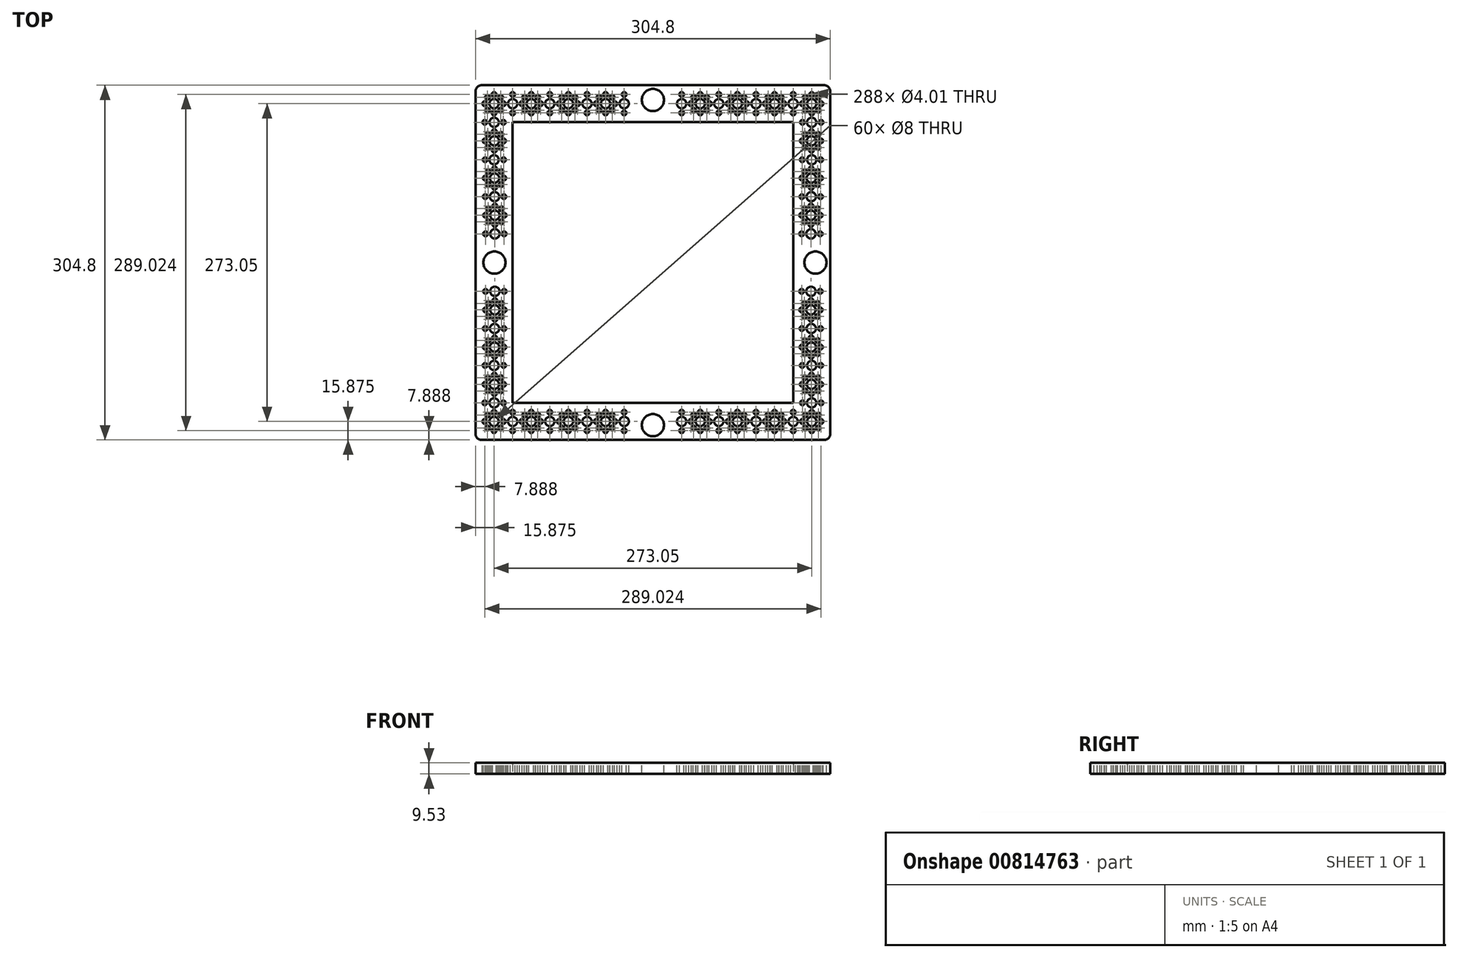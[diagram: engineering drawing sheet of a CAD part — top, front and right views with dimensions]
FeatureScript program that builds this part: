
annotation { "Feature Type Name" : "Feature", "Feature Type Description" : "" }
export const myFeature = defineFeature(function(context is Context, id is Id, definition is map)
    precondition{}
    {
        {
            var Q0;
            Q0=qCreatedBy(makeId("Top.planeOp"),FACE);
            var sketch = newSketch(context, id + "F0", { "sketchPlane" : qUnion([Q0])});
            skLineSegment(sketch, "E0.bottom", {"start": v(152.4, 152.4) * mm, "end": v(-152.4, 152.4) * mm});
            skLineSegment(sketch, "E0.top", {"start": v(152.4, -152.4) * mm, "end": v(-152.4, -152.4) * mm});
            skLineSegment(sketch, "E0.left", {"start": v(152.4, 152.4) * mm, "end": v(152.4, -152.4) * mm});
            skLineSegment(sketch, "E0.right", {"start": v(-152.4, 152.4) * mm, "end": v(-152.4, -152.4) * mm});
            skPoint(sketch, "E0.middle", {"position": v(0, 0) * mm});
            skLineSegment(sketch, "E1.bottom", {"start": v(-120.65, 120.65) * mm, "end": v(120.65, 120.65) * mm});
            skLineSegment(sketch, "E1.top", {"start": v(-120.65, -120.65) * mm, "end": v(120.65, -120.65) * mm});
            skLineSegment(sketch, "E1.left", {"start": v(-120.65, 120.65) * mm, "end": v(-120.65, -120.65) * mm});
            skLineSegment(sketch, "E1.right", {"start": v(120.65, 120.65) * mm, "end": v(120.65, -120.65) * mm});
            skSolve(sketch);
        }
        {
            var Q0;
            Q0=qSketchRegion(id+"F0",true);
            extrude(context, id + "F1", {"entities" : qUnion([Q0]), "depth" : 9.52 * mm, "offsetDistance" : 25.4 * mm});
        }
        {
            var Q0;
            Q0=makeQuery(id+"F1.opExtrude","CAP_FACE",FACE,{"disambiguationData":[OSD([sQuery(id+"F0.wireOp",EDGE,"E0.bottom"),sQuery(id+"F0.wireOp",EDGE,"E0.top"),sQuery(id+"F0.wireOp",EDGE,"E0.left"),sQuery(id+"F0.wireOp",EDGE,"E0.right")])],"isStart":false});
            var sketch = newSketch(context, id + "F2", { "sketchPlane" : qUnion([Q0])});
            skPoint(sketch, "E2", {"position": v(0, 139.7) * mm});
            skPoint(sketch, "E3", {"position": v(139.7, 0) * mm});
            skPoint(sketch, "E4", {"position": v(0, -139.7) * mm});
            skPoint(sketch, "E5", {"position": v(-136.2, 0) * mm});
            skLineSegment(sketch, "E6", {"start": v(0, 120.65) * mm, "end": v(0, 152.4) * mm});
            skSolve(sketch);
        }
        {
            var Q0;
            Q0=sQuery(id+"F2.wireOp",VERTEX,"E2");
            var Q1;
            Q1=sQuery(id+"F2.wireOp",VERTEX,"E3");
            var Q2;
            Q2=sQuery(id+"F2.wireOp",VERTEX,"E4");
            var Q3;
            Q3=sQuery(id+"F2.wireOp",VERTEX,"E5");
            var Q4;
            Q4=makeQuery(id+"F1.opExtrude","SWEPT_BODY",BODY,{"disambiguationData":[OSD([sQuery(id+"F0.wireOp",EDGE,"E0.bottom"),sQuery(id+"F0.wireOp",EDGE,"E0.top"),sQuery(id+"F0.wireOp",EDGE,"E0.left"),sQuery(id+"F0.wireOp",EDGE,"E0.right")])]});
            hole(context, id + "F3", {"style" : HoleStyle.SIMPLE, "endStyle" : HoleEndStyle.THROUGH, "holeDiameter" : 19.05 * mm, "locations" : qUnion([Q0, Q1, Q2, Q3]), "scope" : qUnion([Q4]), "tappedDepth" : 12.7 * mm, "tapClearance" : 3, "majorDiameter" : 6.35 * mm});
        }
        {
            var Q0;
            Q0=makeQuery(id+"F1.opExtrude","SWEPT_EDGE",EDGE,{"disambiguationData":[OSD([sQuery(id+"F0.wireOp",EDGE,"E0.bottom"),sQuery(id+"F0.wireOp",EDGE,"E0.right")])]});
            fillet(context, id + "F4", {"entities" : qUnion([Q0]), "radius" : 5.08 * mm, "tangentPropagation" : true, "allowEdgeOverflow" : false});
        }
        {
            var Q0;
            Q0=makeQuery(id+"F1.opExtrude","SWEPT_EDGE",EDGE,{"disambiguationData":[OSD([sQuery(id+"F0.wireOp",EDGE,"E0.bottom"),sQuery(id+"F0.wireOp",EDGE,"E0.left")])]});
            var Q1;
            Q1=makeQuery(id+"F1.opExtrude","SWEPT_EDGE",EDGE,{"disambiguationData":[OSD([sQuery(id+"F0.wireOp",EDGE,"E0.top"),sQuery(id+"F0.wireOp",EDGE,"E0.left")])]});
            var Q2;
            Q2=makeQuery(id+"F1.opExtrude","SWEPT_EDGE",EDGE,{"disambiguationData":[OSD([sQuery(id+"F0.wireOp",EDGE,"E0.top"),sQuery(id+"F0.wireOp",EDGE,"E0.right")])]});
            fillet(context, id + "F5", {"entities" : qUnion([Q0, Q1, Q2]), "radius" : 5.08 * mm, "tangentPropagation" : true, "allowEdgeOverflow" : false});
        }
        {
            var Q0;
            Q0=makeQuery(id+"F1.opExtrude","CAP_FACE",FACE,{"disambiguationData":[OSD([sQuery(id+"F0.wireOp",EDGE,"E0.bottom"),sQuery(id+"F0.wireOp",EDGE,"E0.top"),sQuery(id+"F0.wireOp",EDGE,"E0.left"),sQuery(id+"F0.wireOp",EDGE,"E0.right")])],"isStart":false});
            var sketch = newSketch(context, id + "F6", { "sketchPlane" : qUnion([Q0])});
            skPoint(sketch, "E7", {"position": v(-136.53, 136.53) * mm});
            skPoint(sketch, "E8", {"position": v(-136.53, 144.51) * mm});
            skPoint(sketch, "E9.1.0", {"position": v(-142.17, 142.17) * mm});
            skPoint(sketch, "E9.2.0", {"position": v(-144.51, 136.52) * mm});
            skPoint(sketch, "E9.3.0", {"position": v(-142.17, 130.88) * mm});
            skPoint(sketch, "E9.4.0", {"position": v(-136.53, 128.54) * mm});
            skPoint(sketch, "E9.5.0", {"position": v(-130.88, 130.88) * mm});
            skPoint(sketch, "E9.6.0", {"position": v(-128.54, 136.53) * mm});
            skPoint(sketch, "E9.7.0", {"position": v(-130.88, 142.17) * mm});
            skPoint(sketch, "E10.1.0.0", {"position": v(-104.58, 136.53) * mm});
            skPoint(sketch, "E10.1.0.1", {"position": v(-104.58, 144.51) * mm});
            skPoint(sketch, "E10.1.0.2", {"position": v(-110.22, 142.17) * mm});
            skPoint(sketch, "E10.1.0.3", {"position": v(-112.56, 136.52) * mm});
            skPoint(sketch, "E10.1.0.4", {"position": v(-110.22, 130.88) * mm});
            skPoint(sketch, "E10.1.0.5", {"position": v(-104.58, 128.54) * mm});
            skPoint(sketch, "E10.1.0.6", {"position": v(-98.93, 130.88) * mm});
            skPoint(sketch, "E10.1.0.7", {"position": v(-96.59, 136.53) * mm});
            skPoint(sketch, "E10.1.0.8", {"position": v(-98.93, 142.17) * mm});
            skPoint(sketch, "E10.2.0.0", {"position": v(-72.63, 136.53) * mm});
            skPoint(sketch, "E10.2.0.1", {"position": v(-72.63, 144.51) * mm});
            skPoint(sketch, "E10.2.0.2", {"position": v(-78.28, 142.17) * mm});
            skPoint(sketch, "E10.2.0.3", {"position": v(-80.62, 136.52) * mm});
            skPoint(sketch, "E10.2.0.4", {"position": v(-78.28, 130.88) * mm});
            skPoint(sketch, "E10.2.0.5", {"position": v(-72.63, 128.54) * mm});
            skPoint(sketch, "E10.2.0.6", {"position": v(-66.98, 130.88) * mm});
            skPoint(sketch, "E10.2.0.7", {"position": v(-64.64, 136.53) * mm});
            skPoint(sketch, "E10.2.0.8", {"position": v(-66.98, 142.17) * mm});
            skPoint(sketch, "E10.3.0.0", {"position": v(-40.68, 136.53) * mm});
            skPoint(sketch, "E10.3.0.1", {"position": v(-40.68, 144.51) * mm});
            skPoint(sketch, "E10.3.0.2", {"position": v(-46.33, 142.17) * mm});
            skPoint(sketch, "E10.3.0.3", {"position": v(-48.67, 136.52) * mm});
            skPoint(sketch, "E10.3.0.4", {"position": v(-46.33, 130.88) * mm});
            skPoint(sketch, "E10.3.0.5", {"position": v(-40.68, 128.54) * mm});
            skPoint(sketch, "E10.3.0.6", {"position": v(-35.03, 130.88) * mm});
            skPoint(sketch, "E10.3.0.7", {"position": v(-32.7, 136.53) * mm});
            skPoint(sketch, "E10.3.0.8", {"position": v(-35.03, 142.17) * mm});
            skLineSegment(sketch, "E10.direction1", {"start": v(-136.53, 136.53) * mm, "end": v(-104.58, 136.53) * mm, "construction": true});
            skPoint(sketch, "E11", {"position": v(-120.55, 136.53) * mm});
            skPoint(sketch, "E12", {"position": v(-88.6, 136.53) * mm});
            skPoint(sketch, "E13", {"position": v(-24.7, 136.53) * mm});
            skPoint(sketch, "E14", {"position": v(-56.65, 136.53) * mm});
            skPoint(sketch, "E15", {"position": v(-56.65, 144.51) * mm});
            skPoint(sketch, "E16", {"position": v(-24.7, 144.51) * mm});
            skPoint(sketch, "E17", {"position": v(-24.7, 128.54) * mm});
            skPoint(sketch, "E18", {"position": v(-56.65, 128.54) * mm});
            skPoint(sketch, "E19", {"position": v(-88.6, 128.54) * mm});
            skPoint(sketch, "E20", {"position": v(-88.6, 144.51) * mm});
            skPoint(sketch, "E21", {"position": v(-120.55, 128.54) * mm});
            skPoint(sketch, "E22", {"position": v(-120.55, 144.51) * mm});
            skPoint(sketch, "E23.MirrorP", {"position": v(96.59, 136.53) * mm});
            skLineSegment(sketch, "E24.MirrorCS", {"start": v(136.53, 136.53) * mm, "end": v(104.58, 136.53) * mm, "construction": true});
            skPoint(sketch, "E25.MirrorP", {"position": v(48.67, 136.52) * mm});
            skPoint(sketch, "E26.MirrorP", {"position": v(64.64, 136.53) * mm});
            skPoint(sketch, "E27.MirrorP", {"position": v(88.6, 136.53) * mm});
            skPoint(sketch, "E28.MirrorP", {"position": v(40.68, 136.53) * mm});
            skPoint(sketch, "E29.MirrorP", {"position": v(32.7, 136.53) * mm});
            skPoint(sketch, "E30.MirrorP", {"position": v(136.53, 136.53) * mm});
            skPoint(sketch, "E31.MirrorP", {"position": v(120.55, 136.53) * mm});
            skPoint(sketch, "E32.MirrorP", {"position": v(98.93, 130.88) * mm});
            skPoint(sketch, "E33.MirrorP", {"position": v(78.28, 142.17) * mm});
            skPoint(sketch, "E34.MirrorP", {"position": v(46.33, 130.88) * mm});
            skPoint(sketch, "E35.MirrorP", {"position": v(120.55, 128.54) * mm});
            skPoint(sketch, "E36.MirrorP", {"position": v(78.28, 130.88) * mm});
            skPoint(sketch, "E37.MirrorP", {"position": v(66.98, 130.88) * mm});
            skPoint(sketch, "E38.MirrorP", {"position": v(110.22, 130.88) * mm});
            skPoint(sketch, "E39.MirrorP", {"position": v(130.88, 142.17) * mm});
            skPoint(sketch, "E40.MirrorP", {"position": v(144.51, 136.52) * mm});
            skPoint(sketch, "E41.MirrorP", {"position": v(56.65, 128.54) * mm});
            skPoint(sketch, "E42.MirrorP", {"position": v(72.63, 136.53) * mm});
            skPoint(sketch, "E43.MirrorP", {"position": v(142.17, 130.88) * mm});
            skPoint(sketch, "E44.MirrorP", {"position": v(40.68, 128.54) * mm});
            skPoint(sketch, "E45.MirrorP", {"position": v(104.58, 144.51) * mm});
            skPoint(sketch, "E46.MirrorP", {"position": v(120.55, 144.51) * mm});
            skPoint(sketch, "E47.MirrorP", {"position": v(98.93, 142.17) * mm});
            skPoint(sketch, "E48.MirrorP", {"position": v(104.58, 128.54) * mm});
            skPoint(sketch, "E49.MirrorP", {"position": v(56.65, 136.53) * mm});
            skPoint(sketch, "E50.MirrorP", {"position": v(72.63, 128.54) * mm});
            skPoint(sketch, "E51.MirrorP", {"position": v(80.62, 136.52) * mm});
            skPoint(sketch, "E52.MirrorP", {"position": v(24.7, 144.51) * mm});
            skPoint(sketch, "E53.MirrorP", {"position": v(35.03, 130.88) * mm});
            skPoint(sketch, "E54.MirrorP", {"position": v(24.7, 128.54) * mm});
            skPoint(sketch, "E55.MirrorP", {"position": v(66.98, 142.17) * mm});
            skPoint(sketch, "E56.MirrorP", {"position": v(72.63, 144.51) * mm});
            skPoint(sketch, "E57.MirrorP", {"position": v(40.68, 144.51) * mm});
            skPoint(sketch, "E58.MirrorP", {"position": v(88.6, 128.54) * mm});
            skPoint(sketch, "E59.MirrorP", {"position": v(35.03, 142.17) * mm});
            skPoint(sketch, "E60.MirrorP", {"position": v(24.7, 136.53) * mm});
            skPoint(sketch, "E61.MirrorP", {"position": v(56.65, 144.51) * mm});
            skPoint(sketch, "E62.MirrorP", {"position": v(46.33, 142.17) * mm});
            skPoint(sketch, "E63.MirrorP", {"position": v(88.6, 144.51) * mm});
            skPoint(sketch, "E64.MirrorP", {"position": v(104.58, 136.53) * mm});
            skPoint(sketch, "E65.MirrorP", {"position": v(128.54, 136.53) * mm});
            skPoint(sketch, "E66.MirrorP", {"position": v(130.88, 130.88) * mm});
            skPoint(sketch, "E67.MirrorP", {"position": v(136.53, 128.54) * mm});
            skPoint(sketch, "E68.MirrorP", {"position": v(136.53, 144.51) * mm});
            skPoint(sketch, "E69.MirrorP", {"position": v(142.17, 142.17) * mm});
            skPoint(sketch, "E70.MirrorP", {"position": v(110.22, 142.17) * mm});
            skPoint(sketch, "E71.MirrorP", {"position": v(112.56, 136.52) * mm});
            skPoint(sketch, "E72.MirrorP", {"position": v(144.51, -136.52) * mm});
            skPoint(sketch, "E73.MirrorP", {"position": v(-88.6, -136.53) * mm});
            skPoint(sketch, "E74.MirrorP", {"position": v(-80.62, -136.52) * mm});
            skPoint(sketch, "E75.MirrorP", {"position": v(-48.67, -136.52) * mm});
            skPoint(sketch, "E76.MirrorP", {"position": v(-40.68, -136.53) * mm});
            skPoint(sketch, "E77.MirrorP", {"position": v(136.53, -136.53) * mm});
            skLineSegment(sketch, "E78.MirrorCS", {"start": v(-136.53, -136.53) * mm, "end": v(-104.58, -136.53) * mm, "construction": true});
            skLineSegment(sketch, "E79.MirrorCS", {"start": v(136.53, -136.53) * mm, "end": v(104.58, -136.53) * mm, "construction": true});
            skPoint(sketch, "E80.MirrorP", {"position": v(-136.53, -136.53) * mm});
            skPoint(sketch, "E81.MirrorP", {"position": v(104.58, -136.53) * mm});
            skPoint(sketch, "E82.MirrorP", {"position": v(-78.28, -142.17) * mm});
            skPoint(sketch, "E83.MirrorP", {"position": v(-96.59, -136.53) * mm});
            skPoint(sketch, "E84.MirrorP", {"position": v(96.59, -136.53) * mm});
            skPoint(sketch, "E85.MirrorP", {"position": v(-136.53, -144.51) * mm});
            skPoint(sketch, "E86.MirrorP", {"position": v(-104.58, -136.53) * mm});
            skPoint(sketch, "E87.MirrorP", {"position": v(120.55, -136.53) * mm});
            skPoint(sketch, "E88.MirrorP", {"position": v(142.17, -142.17) * mm});
            skPoint(sketch, "E89.MirrorP", {"position": v(-110.22, -142.17) * mm});
            skPoint(sketch, "E90.MirrorP", {"position": v(-24.7, -136.53) * mm});
            skPoint(sketch, "E91.MirrorP", {"position": v(-72.63, -144.51) * mm});
            skPoint(sketch, "E92.MirrorP", {"position": v(72.63, -136.53) * mm});
            skPoint(sketch, "E93.MirrorP", {"position": v(56.65, -136.53) * mm});
            skPoint(sketch, "E94.MirrorP", {"position": v(56.65, -144.51) * mm});
            skPoint(sketch, "E95.MirrorP", {"position": v(-112.56, -136.52) * mm});
            skPoint(sketch, "E96.MirrorP", {"position": v(-56.65, -136.53) * mm});
            skPoint(sketch, "E97.MirrorP", {"position": v(-40.68, -144.51) * mm});
            skPoint(sketch, "E98.MirrorP", {"position": v(64.64, -136.53) * mm});
            skPoint(sketch, "E99.MirrorP", {"position": v(-32.7, -136.53) * mm});
            skPoint(sketch, "E100.MirrorP", {"position": v(88.6, -144.51) * mm});
            skPoint(sketch, "E101.MirrorP", {"position": v(104.58, -144.51) * mm});
            skPoint(sketch, "E102.MirrorP", {"position": v(110.22, -130.88) * mm});
            skPoint(sketch, "E103.MirrorP", {"position": v(-120.55, -128.54) * mm});
            skPoint(sketch, "E104.MirrorP", {"position": v(32.7, -136.53) * mm});
            skPoint(sketch, "E105.MirrorP", {"position": v(-104.58, -128.54) * mm});
            skPoint(sketch, "E106.MirrorP", {"position": v(-35.03, -142.17) * mm});
            skPoint(sketch, "E107.MirrorP", {"position": v(80.62, -136.52) * mm});
            skPoint(sketch, "E108.MirrorP", {"position": v(-78.28, -130.88) * mm});
            skPoint(sketch, "E109.MirrorP", {"position": v(120.55, -144.51) * mm});
            skPoint(sketch, "E110.MirrorP", {"position": v(-98.93, -130.88) * mm});
            skPoint(sketch, "E111.MirrorP", {"position": v(-56.65, -144.51) * mm});
            skPoint(sketch, "E112.MirrorP", {"position": v(98.93, -130.88) * mm});
            skPoint(sketch, "E113.MirrorP", {"position": v(-72.63, -136.53) * mm});
            skPoint(sketch, "E114.MirrorP", {"position": v(72.63, -128.54) * mm});
            skPoint(sketch, "E115.MirrorP", {"position": v(128.54, -136.53) * mm});
            skPoint(sketch, "E116.MirrorP", {"position": v(-98.93, -142.17) * mm});
            skPoint(sketch, "E117.MirrorP", {"position": v(-35.03, -130.88) * mm});
            skPoint(sketch, "E118.MirrorP", {"position": v(-66.98, -142.17) * mm});
            skPoint(sketch, "E119.MirrorP", {"position": v(48.67, -136.52) * mm});
            skPoint(sketch, "E120.MirrorP", {"position": v(-24.7, -128.54) * mm});
            skPoint(sketch, "E121.MirrorP", {"position": v(56.65, -128.54) * mm});
            skPoint(sketch, "E122.MirrorP", {"position": v(46.33, -130.88) * mm});
            skPoint(sketch, "E123.MirrorP", {"position": v(40.68, -136.53) * mm});
            skPoint(sketch, "E124.MirrorP", {"position": v(40.68, -128.54) * mm});
            skPoint(sketch, "E125.MirrorP", {"position": v(24.7, -136.53) * mm});
            skPoint(sketch, "E126.MirrorP", {"position": v(136.53, -144.51) * mm});
            skPoint(sketch, "E127.MirrorP", {"position": v(88.6, -136.53) * mm});
            skPoint(sketch, "E128.MirrorP", {"position": v(142.17, -130.88) * mm});
            skPoint(sketch, "E129.MirrorP", {"position": v(35.03, -142.17) * mm});
            skPoint(sketch, "E130.MirrorP", {"position": v(-142.17, -142.17) * mm});
            skPoint(sketch, "E131.MirrorP", {"position": v(-40.68, -128.54) * mm});
            skPoint(sketch, "E132.MirrorP", {"position": v(-64.64, -136.53) * mm});
            skPoint(sketch, "E133.MirrorP", {"position": v(-24.7, -144.51) * mm});
            skPoint(sketch, "E134.MirrorP", {"position": v(78.28, -142.17) * mm});
            skPoint(sketch, "E135.MirrorP", {"position": v(24.7, -144.51) * mm});
            skPoint(sketch, "E136.MirrorP", {"position": v(136.53, -128.54) * mm});
            skPoint(sketch, "E137.MirrorP", {"position": v(120.55, -128.54) * mm});
            skPoint(sketch, "E138.MirrorP", {"position": v(46.33, -142.17) * mm});
            skPoint(sketch, "E139.MirrorP", {"position": v(-66.98, -130.88) * mm});
            skPoint(sketch, "E140.MirrorP", {"position": v(-120.55, -144.51) * mm});
            skPoint(sketch, "E141.MirrorP", {"position": v(130.88, -142.17) * mm});
            skPoint(sketch, "E142.MirrorP", {"position": v(-88.6, -128.54) * mm});
            skPoint(sketch, "E143.MirrorP", {"position": v(104.58, -128.54) * mm});
            skPoint(sketch, "E144.MirrorP", {"position": v(-110.22, -130.88) * mm});
            skPoint(sketch, "E145.MirrorP", {"position": v(-46.33, -142.17) * mm});
            skPoint(sketch, "E146.MirrorP", {"position": v(-88.6, -144.51) * mm});
            skPoint(sketch, "E147.MirrorP", {"position": v(66.98, -130.88) * mm});
            skPoint(sketch, "E148.MirrorP", {"position": v(40.68, -144.51) * mm});
            skPoint(sketch, "E149.MirrorP", {"position": v(-120.55, -136.53) * mm});
            skPoint(sketch, "E150.MirrorP", {"position": v(35.03, -130.88) * mm});
            skPoint(sketch, "E151.MirrorP", {"position": v(-130.88, -142.17) * mm});
            skPoint(sketch, "E152.MirrorP", {"position": v(-128.54, -136.53) * mm});
            skPoint(sketch, "E153.MirrorP", {"position": v(-130.88, -130.88) * mm});
            skPoint(sketch, "E154.MirrorP", {"position": v(-136.53, -128.54) * mm});
            skPoint(sketch, "E155.MirrorP", {"position": v(-142.17, -130.88) * mm});
            skPoint(sketch, "E156.MirrorP", {"position": v(-144.51, -136.52) * mm});
            skPoint(sketch, "E157.MirrorP", {"position": v(72.63, -144.51) * mm});
            skPoint(sketch, "E158.MirrorP", {"position": v(112.56, -136.52) * mm});
            skPoint(sketch, "E159.MirrorP", {"position": v(66.98, -142.17) * mm});
            skPoint(sketch, "E160.MirrorP", {"position": v(78.28, -130.88) * mm});
            skPoint(sketch, "E161.MirrorP", {"position": v(-72.63, -128.54) * mm});
            skPoint(sketch, "E162.MirrorP", {"position": v(98.93, -142.17) * mm});
            skPoint(sketch, "E163.MirrorP", {"position": v(-104.58, -144.51) * mm});
            skPoint(sketch, "E164.MirrorP", {"position": v(24.7, -128.54) * mm});
            skPoint(sketch, "E165.MirrorP", {"position": v(-56.65, -128.54) * mm});
            skPoint(sketch, "E166.MirrorP", {"position": v(130.88, -130.88) * mm});
            skPoint(sketch, "E167.MirrorP", {"position": v(-46.33, -130.88) * mm});
            skPoint(sketch, "E168.MirrorP", {"position": v(88.6, -128.54) * mm});
            skPoint(sketch, "E169.MirrorP", {"position": v(110.22, -142.17) * mm});
            skPoint(sketch, "E170.1.0.0", {"position": v(-136.3, -104.58) * mm});
            skPoint(sketch, "E170.1.0.1", {"position": v(-144.28, -104.58) * mm});
            skPoint(sketch, "E170.1.0.2", {"position": v(-141.94, -110.23) * mm});
            skPoint(sketch, "E170.1.0.3", {"position": v(-141.94, -98.93) * mm});
            skPoint(sketch, "E170.1.0.4", {"position": v(-136.3, -96.6) * mm});
            skPoint(sketch, "E170.1.0.5", {"position": v(-136.3, -112.56) * mm});
            skPoint(sketch, "E170.1.0.6", {"position": v(-130.65, -110.23) * mm});
            skPoint(sketch, "E170.1.0.7", {"position": v(-128.3, -104.58) * mm});
            skPoint(sketch, "E170.1.0.8", {"position": v(-130.65, -98.93) * mm});
            skPoint(sketch, "E170.2.0.0", {"position": v(-136.06, -72.63) * mm});
            skPoint(sketch, "E170.2.0.1", {"position": v(-144.05, -72.63) * mm});
            skPoint(sketch, "E170.2.0.2", {"position": v(-141.7, -78.28) * mm});
            skPoint(sketch, "E170.2.0.3", {"position": v(-141.7, -66.98) * mm});
            skPoint(sketch, "E170.2.0.4", {"position": v(-136.06, -64.64) * mm});
            skPoint(sketch, "E170.2.0.5", {"position": v(-136.06, -80.62) * mm});
            skPoint(sketch, "E170.2.0.6", {"position": v(-130.41, -78.28) * mm});
            skPoint(sketch, "E170.2.0.7", {"position": v(-128.07, -72.63) * mm});
            skPoint(sketch, "E170.2.0.8", {"position": v(-130.41, -66.98) * mm});
            skLineSegment(sketch, "E170.direction1", {"start": v(-136.53, -136.53) * mm, "end": v(-136.3, -104.58) * mm, "construction": true});
            skPoint(sketch, "E171.0.3.0", {"position": v(-135.83, -40.68) * mm});
            skPoint(sketch, "E171.1.3.0", {"position": v(-143.82, -40.68) * mm});
            skPoint(sketch, "E171.2.3.0", {"position": v(-141.48, -46.33) * mm});
            skPoint(sketch, "E171.3.3.0", {"position": v(-141.48, -35.03) * mm});
            skPoint(sketch, "E171.4.3.0", {"position": v(-135.83, -32.7) * mm});
            skPoint(sketch, "E171.5.3.0", {"position": v(-135.83, -48.67) * mm});
            skPoint(sketch, "E171.6.3.0", {"position": v(-130.18, -46.33) * mm});
            skPoint(sketch, "E171.7.3.0", {"position": v(-127.84, -40.68) * mm});
            skPoint(sketch, "E171.8.3.0", {"position": v(-130.18, -35.03) * mm});
            skPoint(sketch, "E172", {"position": v(-136.53, -88.36) * mm});
            skPoint(sketch, "E173", {"position": v(-144.28, -88.36) * mm});
            skPoint(sketch, "E174", {"position": v(-128.3, -88.36) * mm});
            skPoint(sketch, "E175", {"position": v(-136.4, -120.55) * mm});
            skPoint(sketch, "E176", {"position": v(-136.06, -56.66) * mm});
            skPoint(sketch, "E177", {"position": v(-135.83, -24.7) * mm});
            skPoint(sketch, "E178", {"position": v(-144.51, -120.55) * mm});
            skPoint(sketch, "E179", {"position": v(-128.54, -120.55) * mm});
            skPoint(sketch, "E180", {"position": v(-128.07, -56.66) * mm});
            skPoint(sketch, "E181", {"position": v(-144.05, -56.66) * mm});
            skPoint(sketch, "E182", {"position": v(-143.82, -24.7) * mm});
            skPoint(sketch, "E183", {"position": v(-127.84, -24.7) * mm});
            skPoint(sketch, "E184.MirrorP", {"position": v(-144.28, 104.58) * mm});
            skPoint(sketch, "E185.MirrorP", {"position": v(-130.65, 98.93) * mm});
            skPoint(sketch, "E186.MirrorP", {"position": v(-130.18, 46.33) * mm});
            skPoint(sketch, "E187.MirrorP", {"position": v(-144.51, 120.55) * mm});
            skPoint(sketch, "E188.MirrorP", {"position": v(-141.94, 110.23) * mm});
            skPoint(sketch, "E189.MirrorP", {"position": v(-143.82, 40.68) * mm});
            skPoint(sketch, "E190.MirrorP", {"position": v(-141.48, 46.33) * mm});
            skPoint(sketch, "E191.MirrorP", {"position": v(-144.05, 56.66) * mm});
            skPoint(sketch, "E192.MirrorP", {"position": v(-136.3, 96.6) * mm});
            skPoint(sketch, "E193.MirrorP", {"position": v(-136.53, 88.36) * mm});
            skPoint(sketch, "E194.MirrorP", {"position": v(-141.7, 78.28) * mm});
            skPoint(sketch, "E195.MirrorP", {"position": v(-128.3, 104.58) * mm});
            skPoint(sketch, "E196.MirrorP", {"position": v(-136.3, 104.58) * mm});
            skPoint(sketch, "E197.MirrorP", {"position": v(-135.83, 48.67) * mm});
            skPoint(sketch, "E198.MirrorP", {"position": v(-128.07, 72.63) * mm});
            skPoint(sketch, "E199.MirrorP", {"position": v(-135.83, 24.7) * mm});
            skPoint(sketch, "E200.MirrorP", {"position": v(-128.3, 88.36) * mm});
            skLineSegment(sketch, "E201.MirrorCS", {"start": v(-136.53, 136.53) * mm, "end": v(-136.3, 104.58) * mm, "construction": true});
            skPoint(sketch, "E202.MirrorP", {"position": v(-136.06, 80.62) * mm});
            skPoint(sketch, "E203.MirrorP", {"position": v(-141.7, 66.98) * mm});
            skPoint(sketch, "E204.MirrorP", {"position": v(-130.65, 110.23) * mm});
            skPoint(sketch, "E205.MirrorP", {"position": v(-135.83, 32.7) * mm});
            skPoint(sketch, "E206.MirrorP", {"position": v(-136.06, 72.63) * mm});
            skPoint(sketch, "E207.MirrorP", {"position": v(-144.05, 72.63) * mm});
            skPoint(sketch, "E208.MirrorP", {"position": v(-130.18, 35.03) * mm});
            skPoint(sketch, "E209.MirrorP", {"position": v(-141.48, 35.03) * mm});
            skPoint(sketch, "E210.MirrorP", {"position": v(-143.82, 24.7) * mm});
            skPoint(sketch, "E211.MirrorP", {"position": v(-136.3, 112.56) * mm});
            skPoint(sketch, "E212.MirrorP", {"position": v(-136.06, 64.64) * mm});
            skPoint(sketch, "E213.MirrorP", {"position": v(-130.41, 78.28) * mm});
            skPoint(sketch, "E214.MirrorP", {"position": v(-136.4, 120.55) * mm});
            skPoint(sketch, "E215.MirrorP", {"position": v(-144.28, 88.36) * mm});
            skPoint(sketch, "E216.MirrorP", {"position": v(-136.06, 56.66) * mm});
            skPoint(sketch, "E217.MirrorP", {"position": v(-127.84, 24.7) * mm});
            skPoint(sketch, "E218.MirrorP", {"position": v(-130.41, 66.98) * mm});
            skPoint(sketch, "E219.MirrorP", {"position": v(-128.54, 120.55) * mm});
            skPoint(sketch, "E220.MirrorP", {"position": v(-135.83, 40.68) * mm});
            skPoint(sketch, "E221.MirrorP", {"position": v(-127.84, 40.68) * mm});
            skPoint(sketch, "E222.MirrorP", {"position": v(-128.07, 56.66) * mm});
            skPoint(sketch, "E223.MirrorP", {"position": v(-141.94, 98.93) * mm});
            skPoint(sketch, "E224.MirrorP", {"position": v(143.82, 40.68) * mm});
            skPoint(sketch, "E225.MirrorP", {"position": v(135.83, -48.67) * mm});
            skPoint(sketch, "E226.MirrorP", {"position": v(141.94, 98.93) * mm});
            skPoint(sketch, "E227.MirrorP", {"position": v(136.3, 112.56) * mm});
            skPoint(sketch, "E228.MirrorP", {"position": v(135.83, 40.68) * mm});
            skPoint(sketch, "E229.MirrorP", {"position": v(130.18, -46.33) * mm});
            skPoint(sketch, "E230.MirrorP", {"position": v(136.06, 64.64) * mm});
            skPoint(sketch, "E231.MirrorP", {"position": v(141.7, 78.28) * mm});
            skPoint(sketch, "E232.MirrorP", {"position": v(130.18, 46.33) * mm});
            skPoint(sketch, "E233.MirrorP", {"position": v(144.05, -72.63) * mm});
            skPoint(sketch, "E234.MirrorP", {"position": v(135.83, -24.7) * mm});
            skPoint(sketch, "E235.MirrorP", {"position": v(141.48, 35.03) * mm});
            skPoint(sketch, "E236.MirrorP", {"position": v(141.7, -78.28) * mm});
            skPoint(sketch, "E237.MirrorP", {"position": v(143.82, -40.68) * mm});
            skPoint(sketch, "E238.MirrorP", {"position": v(136.3, 96.6) * mm});
            skPoint(sketch, "E239.MirrorP", {"position": v(144.28, -104.58) * mm});
            skPoint(sketch, "E240.MirrorP", {"position": v(130.41, 66.98) * mm});
            skPoint(sketch, "E241.MirrorP", {"position": v(136.06, 72.63) * mm});
            skPoint(sketch, "E242.MirrorP", {"position": v(144.05, 72.63) * mm});
            skPoint(sketch, "E243.MirrorP", {"position": v(136.53, 88.36) * mm});
            skPoint(sketch, "E244.MirrorP", {"position": v(135.83, -40.68) * mm});
            skPoint(sketch, "E245.MirrorP", {"position": v(130.65, 98.93) * mm});
            skPoint(sketch, "E246.MirrorP", {"position": v(136.06, -72.63) * mm});
            skPoint(sketch, "E247.MirrorP", {"position": v(136.3, -104.58) * mm});
            skPoint(sketch, "E248.MirrorP", {"position": v(136.3, -112.56) * mm});
            skPoint(sketch, "E249.MirrorP", {"position": v(136.06, -80.62) * mm});
            skPoint(sketch, "E250.MirrorP", {"position": v(141.48, -35.03) * mm});
            skPoint(sketch, "E251.MirrorP", {"position": v(136.4, -120.55) * mm});
            skPoint(sketch, "E252.MirrorP", {"position": v(143.82, -24.7) * mm});
            skPoint(sketch, "E253.MirrorP", {"position": v(136.3, 104.58) * mm});
            skPoint(sketch, "E254.MirrorP", {"position": v(128.07, 72.63) * mm});
            skPoint(sketch, "E255.MirrorP", {"position": v(141.7, -66.98) * mm});
            skPoint(sketch, "E256.MirrorP", {"position": v(144.51, 120.55) * mm});
            skPoint(sketch, "E257.MirrorP", {"position": v(136.4, 120.55) * mm});
            skPoint(sketch, "E258.MirrorP", {"position": v(136.06, 80.62) * mm});
            skPoint(sketch, "E259.MirrorP", {"position": v(130.65, 110.23) * mm});
            skPoint(sketch, "E260.MirrorP", {"position": v(130.65, -98.93) * mm});
            skPoint(sketch, "E261.MirrorP", {"position": v(135.83, 24.7) * mm});
            skPoint(sketch, "E262.MirrorP", {"position": v(144.28, 104.58) * mm});
            skPoint(sketch, "E263.MirrorP", {"position": v(128.54, -120.55) * mm});
            skPoint(sketch, "E264.MirrorP", {"position": v(128.3, -88.36) * mm});
            skPoint(sketch, "E265.MirrorP", {"position": v(141.94, 110.23) * mm});
            skPoint(sketch, "E266.MirrorP", {"position": v(127.84, -40.68) * mm});
            skPoint(sketch, "E267.MirrorP", {"position": v(136.06, -56.66) * mm});
            skPoint(sketch, "E268.MirrorP", {"position": v(135.83, 48.67) * mm});
            skPoint(sketch, "E269.MirrorP", {"position": v(144.05, 56.66) * mm});
            skPoint(sketch, "E270.MirrorP", {"position": v(128.07, -72.63) * mm});
            skPoint(sketch, "E271.MirrorP", {"position": v(128.3, -104.58) * mm});
            skPoint(sketch, "E272.MirrorP", {"position": v(135.83, 32.7) * mm});
            skPoint(sketch, "E273.MirrorP", {"position": v(127.84, 40.68) * mm});
            skPoint(sketch, "E274.MirrorP", {"position": v(144.28, 88.36) * mm});
            skPoint(sketch, "E275.MirrorP", {"position": v(136.53, -88.36) * mm});
            skPoint(sketch, "E276.MirrorP", {"position": v(136.3, -96.6) * mm});
            skPoint(sketch, "E277.MirrorP", {"position": v(136.06, -64.64) * mm});
            skPoint(sketch, "E278.MirrorP", {"position": v(141.48, -46.33) * mm});
            skPoint(sketch, "E279.MirrorP", {"position": v(144.05, -56.66) * mm});
            skPoint(sketch, "E280.MirrorP", {"position": v(128.07, -56.66) * mm});
            skPoint(sketch, "E281.MirrorP", {"position": v(141.94, -98.93) * mm});
            skPoint(sketch, "E282.MirrorP", {"position": v(130.18, 35.03) * mm});
            skPoint(sketch, "E283.MirrorP", {"position": v(144.51, -120.55) * mm});
            skPoint(sketch, "E284.MirrorP", {"position": v(130.41, -66.98) * mm});
            skPoint(sketch, "E285.MirrorP", {"position": v(128.54, 120.55) * mm});
            skPoint(sketch, "E286.MirrorP", {"position": v(130.18, -35.03) * mm});
            skPoint(sketch, "E287.MirrorP", {"position": v(141.94, -110.23) * mm});
            skPoint(sketch, "E288.MirrorP", {"position": v(128.3, 104.58) * mm});
            skPoint(sketch, "E289.MirrorP", {"position": v(128.3, 88.36) * mm});
            skPoint(sketch, "E290.MirrorP", {"position": v(130.41, 78.28) * mm});
            skPoint(sketch, "E291.MirrorP", {"position": v(127.84, -24.7) * mm});
            skPoint(sketch, "E292.MirrorP", {"position": v(141.48, 46.33) * mm});
            skPoint(sketch, "E293.MirrorP", {"position": v(127.84, 24.7) * mm});
            skPoint(sketch, "E294.MirrorP", {"position": v(141.7, 66.98) * mm});
            skPoint(sketch, "E295.MirrorP", {"position": v(144.28, -88.36) * mm});
            skPoint(sketch, "E296.MirrorP", {"position": v(130.41, -78.28) * mm});
            skPoint(sketch, "E297.MirrorP", {"position": v(135.83, -32.7) * mm});
            skPoint(sketch, "E298.MirrorP", {"position": v(130.65, -110.23) * mm});
            skPoint(sketch, "E299.MirrorP", {"position": v(136.06, 56.66) * mm});
            skPoint(sketch, "E300.MirrorP", {"position": v(128.07, 56.66) * mm});
            skPoint(sketch, "E301.MirrorP", {"position": v(143.82, 24.7) * mm});
            skPoint(sketch, "E302", {"position": v(-88.6, 88.36) * mm});
            skPoint(sketch, "E303", {"position": v(-96.59, 88.36) * mm});
            skPoint(sketch, "E304.1.0", {"position": v(-94.25, 82.71) * mm});
            skPoint(sketch, "E304.2.0", {"position": v(-88.6, 80.37) * mm});
            skPoint(sketch, "E304.3.0", {"position": v(-82.95, 82.71) * mm});
            skPoint(sketch, "E304.4.0", {"position": v(-80.62, 88.36) * mm});
            skPoint(sketch, "E304.5.0", {"position": v(-82.95, 94) * mm});
            skPoint(sketch, "E304.6.0", {"position": v(-88.6, 96.35) * mm});
            skPoint(sketch, "E304.7.0", {"position": v(-94.25, 94) * mm});
            skPoint(sketch, "E305.0.1.0", {"position": v(-88.6, 16.48) * mm});
            skPoint(sketch, "E305.0.1.1", {"position": v(-94.25, 18.82) * mm});
            skPoint(sketch, "E305.0.1.2", {"position": v(-82.95, 30.11) * mm});
            skPoint(sketch, "E305.0.1.3", {"position": v(-80.62, 24.46) * mm});
            skPoint(sketch, "E305.0.1.4", {"position": v(-94.25, 30.11) * mm});
            skPoint(sketch, "E305.0.1.5", {"position": v(-82.95, 18.82) * mm});
            skPoint(sketch, "E305.0.1.6", {"position": v(-88.6, 32.45) * mm});
            skPoint(sketch, "E305.0.1.7", {"position": v(-88.6, 24.46) * mm});
            skPoint(sketch, "E305.0.1.8", {"position": v(-96.59, 24.46) * mm});
            skPoint(sketch, "E305.0.1.9", {"position": v(-88.6, 24.46) * mm});
            skPoint(sketch, "E305.1.0.0", {"position": v(-24.7, 80.37) * mm});
            skPoint(sketch, "E305.1.0.1", {"position": v(-30.35, 82.71) * mm});
            skPoint(sketch, "E305.1.0.2", {"position": v(-19.06, 94) * mm});
            skPoint(sketch, "E305.1.0.3", {"position": v(-16.72, 88.36) * mm});
            skPoint(sketch, "E305.1.0.4", {"position": v(-30.35, 94) * mm});
            skPoint(sketch, "E305.1.0.5", {"position": v(-19.06, 82.71) * mm});
            skPoint(sketch, "E305.1.0.6", {"position": v(-24.7, 96.35) * mm});
            skPoint(sketch, "E305.1.0.7", {"position": v(-24.7, 88.36) * mm});
            skPoint(sketch, "E305.1.0.8", {"position": v(-32.7, 88.36) * mm});
            skPoint(sketch, "E305.1.0.9", {"position": v(-24.7, 88.36) * mm});
            skPoint(sketch, "E305.1.1.0", {"position": v(-24.7, 16.48) * mm});
            skPoint(sketch, "E305.1.1.1", {"position": v(-30.35, 18.82) * mm});
            skPoint(sketch, "E305.1.1.2", {"position": v(-19.06, 30.11) * mm});
            skPoint(sketch, "E305.1.1.3", {"position": v(-16.72, 24.46) * mm});
            skPoint(sketch, "E305.1.1.4", {"position": v(-30.35, 30.11) * mm});
            skPoint(sketch, "E305.1.1.5", {"position": v(-19.06, 18.82) * mm});
            skPoint(sketch, "E305.1.1.6", {"position": v(-24.7, 32.45) * mm});
            skPoint(sketch, "E305.1.1.7", {"position": v(-24.7, 24.46) * mm});
            skPoint(sketch, "E305.1.1.8", {"position": v(-32.7, 24.46) * mm});
            skPoint(sketch, "E305.1.1.9", {"position": v(-24.7, 24.46) * mm});
            skLineSegment(sketch, "E305.direction1", {"start": v(-94.25, 82.71) * mm, "end": v(-30.35, 82.71) * mm, "construction": true});
            skLineSegment(sketch, "E305.direction2", {"start": v(-94.25, 82.71) * mm, "end": v(-94.25, 18.82) * mm, "construction": true});
            skPoint(sketch, "E306.MirrorP", {"position": v(88.6, 24.46) * mm});
            skPoint(sketch, "E307.MirrorP", {"position": v(88.6, 88.36) * mm});
            skPoint(sketch, "E308.MirrorP", {"position": v(96.59, 88.36) * mm});
            skPoint(sketch, "E309.MirrorP", {"position": v(24.7, 24.46) * mm});
            skPoint(sketch, "E310.MirrorP", {"position": v(96.59, 24.46) * mm});
            skPoint(sketch, "E311.MirrorP", {"position": v(24.7, 88.36) * mm});
            skPoint(sketch, "E312.MirrorP", {"position": v(19.06, 82.71) * mm});
            skPoint(sketch, "E313.MirrorP", {"position": v(88.6, 32.45) * mm});
            skPoint(sketch, "E314.MirrorP", {"position": v(19.06, 30.11) * mm});
            skPoint(sketch, "E315.MirrorP", {"position": v(30.35, 94) * mm});
            skPoint(sketch, "E316.MirrorP", {"position": v(30.35, 18.82) * mm});
            skPoint(sketch, "E317.MirrorP", {"position": v(94.25, 18.82) * mm});
            skPoint(sketch, "E318.MirrorP", {"position": v(80.62, 24.46) * mm});
            skPoint(sketch, "E319.MirrorP", {"position": v(19.06, 94) * mm});
            skPoint(sketch, "E320.MirrorP", {"position": v(19.06, 18.82) * mm});
            skPoint(sketch, "E321.MirrorP", {"position": v(82.95, 94) * mm});
            skPoint(sketch, "E322.MirrorP", {"position": v(32.7, 24.46) * mm});
            skPoint(sketch, "E323.MirrorP", {"position": v(24.7, 16.48) * mm});
            skPoint(sketch, "E324.MirrorP", {"position": v(94.25, 30.11) * mm});
            skPoint(sketch, "E325.MirrorP", {"position": v(30.35, 30.11) * mm});
            skPoint(sketch, "E326.MirrorP", {"position": v(24.7, 96.35) * mm});
            skPoint(sketch, "E327.MirrorP", {"position": v(16.72, 24.46) * mm});
            skPoint(sketch, "E328.MirrorP", {"position": v(94.25, 82.71) * mm});
            skPoint(sketch, "E329.MirrorP", {"position": v(88.6, 16.48) * mm});
            skLineSegment(sketch, "E330.MirrorCS", {"start": v(94.25, 82.71) * mm, "end": v(94.25, 18.82) * mm, "construction": true});
            skPoint(sketch, "E331.MirrorP", {"position": v(30.35, 82.71) * mm});
            skPoint(sketch, "E332.MirrorP", {"position": v(80.62, 88.36) * mm});
            skPoint(sketch, "E333.MirrorP", {"position": v(16.72, 88.36) * mm});
            skPoint(sketch, "E334.MirrorP", {"position": v(24.7, 32.45) * mm});
            skPoint(sketch, "E335.MirrorP", {"position": v(24.7, 80.37) * mm});
            skPoint(sketch, "E336.MirrorP", {"position": v(82.95, 18.82) * mm});
            skPoint(sketch, "E337.MirrorP", {"position": v(94.25, 94) * mm});
            skPoint(sketch, "E338.MirrorP", {"position": v(32.7, 88.36) * mm});
            skPoint(sketch, "E339.MirrorP", {"position": v(82.95, 30.11) * mm});
            skPoint(sketch, "E340.MirrorP", {"position": v(82.95, 82.71) * mm});
            skLineSegment(sketch, "E341.MirrorCS", {"start": v(94.25, 82.71) * mm, "end": v(30.35, 82.71) * mm, "construction": true});
            skPoint(sketch, "E342.MirrorP", {"position": v(88.6, 96.35) * mm});
            skPoint(sketch, "E343.MirrorP", {"position": v(88.6, 80.37) * mm});
            skPoint(sketch, "E344.MirrorP", {"position": v(88.6, -88.36) * mm});
            skPoint(sketch, "E345.MirrorP", {"position": v(88.6, -24.46) * mm});
            skPoint(sketch, "E346.MirrorP", {"position": v(24.7, -24.46) * mm});
            skPoint(sketch, "E347.MirrorP", {"position": v(24.7, -88.36) * mm});
            skPoint(sketch, "E348.MirrorP", {"position": v(88.6, -80.37) * mm});
            skPoint(sketch, "E349.MirrorP", {"position": v(82.95, -94) * mm});
            skPoint(sketch, "E350.MirrorP", {"position": v(88.6, -96.35) * mm});
            skLineSegment(sketch, "E351.MirrorCS", {"start": v(94.25, -82.71) * mm, "end": v(94.25, -18.82) * mm, "construction": true});
            skPoint(sketch, "E352.MirrorP", {"position": v(80.62, -88.36) * mm});
            skPoint(sketch, "E353.MirrorP", {"position": v(96.59, -88.36) * mm});
            skPoint(sketch, "E354.MirrorP", {"position": v(94.25, -94) * mm});
            skPoint(sketch, "E355.MirrorP", {"position": v(82.95, -82.71) * mm});
            skLineSegment(sketch, "E356.MirrorCS", {"start": v(94.25, -82.71) * mm, "end": v(30.35, -82.71) * mm, "construction": true});
            skPoint(sketch, "E357.MirrorP", {"position": v(94.25, -82.71) * mm});
            skPoint(sketch, "E358.MirrorP", {"position": v(24.7, -80.37) * mm});
            skPoint(sketch, "E359.MirrorP", {"position": v(19.06, -30.11) * mm});
            skPoint(sketch, "E360.MirrorP", {"position": v(88.6, -16.48) * mm});
            skPoint(sketch, "E361.MirrorP", {"position": v(82.95, -18.82) * mm});
            skPoint(sketch, "E362.MirrorP", {"position": v(96.59, -24.46) * mm});
            skPoint(sketch, "E363.MirrorP", {"position": v(30.35, -82.71) * mm});
            skPoint(sketch, "E364.MirrorP", {"position": v(-24.7, -24.46) * mm});
            skPoint(sketch, "E365.MirrorP", {"position": v(80.62, -24.46) * mm});
            skPoint(sketch, "E366.MirrorP", {"position": v(19.06, -82.71) * mm});
            skPoint(sketch, "E367.MirrorP", {"position": v(24.7, -16.48) * mm});
            skPoint(sketch, "E368.MirrorP", {"position": v(32.7, -88.36) * mm});
            skPoint(sketch, "E369.MirrorP", {"position": v(-88.6, -24.46) * mm});
            skPoint(sketch, "E370.MirrorP", {"position": v(30.35, -18.82) * mm});
            skPoint(sketch, "E371.MirrorP", {"position": v(94.25, -30.11) * mm});
            skPoint(sketch, "E372.MirrorP", {"position": v(82.95, -30.11) * mm});
            skPoint(sketch, "E373.MirrorP", {"position": v(30.35, -94) * mm});
            skPoint(sketch, "E374.MirrorP", {"position": v(94.25, -18.82) * mm});
            skPoint(sketch, "E375.MirrorP", {"position": v(-24.7, -88.36) * mm});
            skPoint(sketch, "E376.MirrorP", {"position": v(19.06, -94) * mm});
            skPoint(sketch, "E377.MirrorP", {"position": v(88.6, -32.45) * mm});
            skPoint(sketch, "E378.MirrorP", {"position": v(16.72, -88.36) * mm});
            skPoint(sketch, "E379.MirrorP", {"position": v(30.35, -30.11) * mm});
            skPoint(sketch, "E380.MirrorP", {"position": v(24.7, -96.35) * mm});
            skPoint(sketch, "E381.MirrorP", {"position": v(24.7, -32.45) * mm});
            skPoint(sketch, "E382.MirrorP", {"position": v(16.72, -24.46) * mm});
            skPoint(sketch, "E383.MirrorP", {"position": v(32.7, -24.46) * mm});
            skPoint(sketch, "E384.MirrorP", {"position": v(19.06, -18.82) * mm});
            skPoint(sketch, "E385.MirrorP", {"position": v(-88.6, -88.36) * mm});
            skPoint(sketch, "E386.MirrorP", {"position": v(-30.35, -18.82) * mm});
            skPoint(sketch, "E387.MirrorP", {"position": v(-82.95, -18.82) * mm});
            skPoint(sketch, "E388.MirrorP", {"position": v(-32.7, -24.46) * mm});
            skPoint(sketch, "E389.MirrorP", {"position": v(-19.06, -30.11) * mm});
            skPoint(sketch, "E390.MirrorP", {"position": v(-94.25, -18.82) * mm});
            skPoint(sketch, "E391.MirrorP", {"position": v(-30.35, -94) * mm});
            skPoint(sketch, "E392.MirrorP", {"position": v(-19.06, -18.82) * mm});
            skPoint(sketch, "E393.MirrorP", {"position": v(-16.72, -24.46) * mm});
            skPoint(sketch, "E394.MirrorP", {"position": v(-96.59, -88.36) * mm});
            skPoint(sketch, "E395.MirrorP", {"position": v(-30.35, -30.11) * mm});
            skPoint(sketch, "E396.MirrorP", {"position": v(-88.6, -80.37) * mm});
            skLineSegment(sketch, "E397.MirrorCS", {"start": v(-94.25, -82.71) * mm, "end": v(-94.25, -18.82) * mm, "construction": true});
            skPoint(sketch, "E398.MirrorP", {"position": v(-96.59, -24.46) * mm});
            skPoint(sketch, "E399.MirrorP", {"position": v(-94.25, -82.71) * mm});
            skPoint(sketch, "E400.MirrorP", {"position": v(-88.6, -16.48) * mm});
            skPoint(sketch, "E401.MirrorP", {"position": v(-24.7, -16.48) * mm});
            skPoint(sketch, "E402.MirrorP", {"position": v(-82.95, -82.71) * mm});
            skPoint(sketch, "E403.MirrorP", {"position": v(-24.7, -32.45) * mm});
            skPoint(sketch, "E404.MirrorP", {"position": v(-24.7, -80.37) * mm});
            skPoint(sketch, "E405.MirrorP", {"position": v(-80.62, -88.36) * mm});
            skPoint(sketch, "E406.MirrorP", {"position": v(-80.62, -24.46) * mm});
            skPoint(sketch, "E407.MirrorP", {"position": v(-16.72, -88.36) * mm});
            skPoint(sketch, "E408.MirrorP", {"position": v(-19.06, -82.71) * mm});
            skPoint(sketch, "E409.MirrorP", {"position": v(-24.7, -96.35) * mm});
            skPoint(sketch, "E410.MirrorP", {"position": v(-30.35, -82.71) * mm});
            skPoint(sketch, "E411.MirrorP", {"position": v(-32.7, -88.36) * mm});
            skPoint(sketch, "E412.MirrorP", {"position": v(-82.95, -30.11) * mm});
            skPoint(sketch, "E413.MirrorP", {"position": v(-88.6, -96.35) * mm});
            skPoint(sketch, "E414.MirrorP", {"position": v(-94.25, -30.11) * mm});
            skPoint(sketch, "E415.MirrorP", {"position": v(-82.95, -94) * mm});
            skPoint(sketch, "E416.MirrorP", {"position": v(-19.06, -94) * mm});
            skLineSegment(sketch, "E417.MirrorCS", {"start": v(-94.25, -82.71) * mm, "end": v(-30.35, -82.71) * mm, "construction": true});
            skPoint(sketch, "E418.MirrorP", {"position": v(-94.25, -94) * mm});
            skPoint(sketch, "E419.MirrorP", {"position": v(-88.6, -32.45) * mm});
            skSolve(sketch);
        }
        {
            var Q0;
            Q0=sQuery(id+"F6.wireOp",VERTEX,"E145.MirrorP");
            var Q1;
            Q1=sQuery(id+"F6.wireOp",VERTEX,"E161.MirrorP");
            var Q2;
            Q2=sQuery(id+"F6.wireOp",VERTEX,"E170.1.0.7");
            var Q3;
            Q3=sQuery(id+"F6.wireOp",VERTEX,"E170.2.0.5");
            var Q4;
            Q4=sQuery(id+"F6.wireOp",VERTEX,"E120.MirrorP");
            var Q5;
            Q5=sQuery(id+"F6.wireOp",VERTEX,"E152.MirrorP");
            var Q6;
            Q6=sQuery(id+"F6.wireOp",VERTEX,"E89.MirrorP");
            var Q7;
            Q7=sQuery(id+"F6.wireOp",VERTEX,"E153.MirrorP");
            var Q8;
            Q8=sQuery(id+"F6.wireOp",VERTEX,"E105.MirrorP");
            var Q9;
            Q9=sQuery(id+"F6.wireOp",VERTEX,"E170.2.0.6");
            var Q10;
            Q10=sQuery(id+"F6.wireOp",VERTEX,"E179");
            var Q11;
            Q11=sQuery(id+"F6.wireOp",VERTEX,"E133.MirrorP");
            var Q12;
            Q12=sQuery(id+"F6.wireOp",VERTEX,"E180");
            var Q13;
            Q13=sQuery(id+"F6.wireOp",VERTEX,"E170.1.0.3");
            var Q14;
            Q14=sQuery(id+"F6.wireOp",VERTEX,"E174");
            var Q15;
            Q15=sQuery(id+"F6.wireOp",VERTEX,"E170.1.0.6");
            var Q16;
            Q16=sQuery(id+"F6.wireOp",VERTEX,"E106.MirrorP");
            var Q17;
            Q17=sQuery(id+"F6.wireOp",VERTEX,"E170.2.0.7");
            var Q18;
            Q18=sQuery(id+"F6.wireOp",VERTEX,"E110.MirrorP");
            var Q19;
            Q19=sQuery(id+"F6.wireOp",VERTEX,"E95.MirrorP");
            var Q20;
            Q20=sQuery(id+"F6.wireOp",VERTEX,"E154.MirrorP");
            var Q21;
            Q21=sQuery(id+"F6.wireOp",VERTEX,"E116.MirrorP");
            var Q22;
            Q22=sQuery(id+"F6.wireOp",VERTEX,"E131.MirrorP");
            var Q23;
            Q23=sQuery(id+"F6.wireOp",VERTEX,"E171.7.3.0");
            var Q24;
            Q24=sQuery(id+"F6.wireOp",VERTEX,"E85.MirrorP");
            var Q25;
            Q25=sQuery(id+"F6.wireOp",VERTEX,"E111.MirrorP");
            var Q26;
            Q26=sQuery(id+"F6.wireOp",VERTEX,"E178");
            var Q27;
            Q27=sQuery(id+"F6.wireOp",VERTEX,"E170.2.0.8");
            var Q28;
            Q28=sQuery(id+"F6.wireOp",VERTEX,"E156.MirrorP");
            var Q29;
            Q29=sQuery(id+"F6.wireOp",VERTEX,"E140.MirrorP");
            var Q30;
            Q30=sQuery(id+"F6.wireOp",VERTEX,"E108.MirrorP");
            var Q31;
            Q31=sQuery(id+"F6.wireOp",VERTEX,"E167.MirrorP");
            var Q32;
            Q32=sQuery(id+"F6.wireOp",VERTEX,"E130.MirrorP");
            var Q33;
            Q33=sQuery(id+"F6.wireOp",VERTEX,"E144.MirrorP");
            var Q34;
            Q34=sQuery(id+"F6.wireOp",VERTEX,"E183");
            var Q35;
            Q35=sQuery(id+"F6.wireOp",VERTEX,"E171.4.3.0");
            var Q36;
            Q36=sQuery(id+"F6.wireOp",VERTEX,"E155.MirrorP");
            var Q37;
            Q37=sQuery(id+"F6.wireOp",VERTEX,"E139.MirrorP");
            var Q38;
            Q38=sQuery(id+"F6.wireOp",VERTEX,"E142.MirrorP");
            var Q39;
            Q39=sQuery(id+"F6.wireOp",VERTEX,"E91.MirrorP");
            var Q40;
            Q40=sQuery(id+"F6.wireOp",VERTEX,"E171.8.3.0");
            var Q41;
            Q41=sQuery(id+"F6.wireOp",VERTEX,"E103.MirrorP");
            var Q42;
            Q42=sQuery(id+"F6.wireOp",VERTEX,"E151.MirrorP");
            var Q43;
            Q43=sQuery(id+"F6.wireOp",VERTEX,"E182");
            var Q44;
            Q44=sQuery(id+"F6.wireOp",VERTEX,"E171.3.3.0");
            var Q45;
            Q45=sQuery(id+"F6.wireOp",VERTEX,"E170.2.0.2");
            var Q46;
            Q46=sQuery(id+"F6.wireOp",VERTEX,"E165.MirrorP");
            var Q47;
            Q47=sQuery(id+"F6.wireOp",VERTEX,"E170.1.0.5");
            var Q48;
            Q48=sQuery(id+"F6.wireOp",VERTEX,"E117.MirrorP");
            var Q49;
            Q49=sQuery(id+"F6.wireOp",VERTEX,"E170.1.0.2");
            var Q50;
            Q50=sQuery(id+"F6.wireOp",VERTEX,"E82.MirrorP");
            var Q51;
            Q51=sQuery(id+"F6.wireOp",VERTEX,"E173");
            var Q52;
            Q52=sQuery(id+"F6.wireOp",VERTEX,"E170.2.0.3");
            var Q53;
            Q53=sQuery(id+"F6.wireOp",VERTEX,"E170.1.0.4");
            var Q54;
            Q54=sQuery(id+"F6.wireOp",VERTEX,"E146.MirrorP");
            var Q55;
            Q55=sQuery(id+"F6.wireOp",VERTEX,"E171.2.3.0");
            var Q56;
            Q56=sQuery(id+"F6.wireOp",VERTEX,"E181");
            var Q57;
            Q57=sQuery(id+"F6.wireOp",VERTEX,"E170.1.0.8");
            var Q58;
            Q58=sQuery(id+"F6.wireOp",VERTEX,"E171.6.3.0");
            var Q59;
            Q59=sQuery(id+"F6.wireOp",VERTEX,"E171.5.3.0");
            var Q60;
            Q60=sQuery(id+"F6.wireOp",VERTEX,"E83.MirrorP");
            var Q61;
            Q61=sQuery(id+"F6.wireOp",VERTEX,"E97.MirrorP");
            var Q62;
            Q62=sQuery(id+"F6.wireOp",VERTEX,"E171.1.3.0");
            var Q63;
            Q63=sQuery(id+"F6.wireOp",VERTEX,"E170.2.0.4");
            var Q64;
            Q64=sQuery(id+"F6.wireOp",VERTEX,"E75.MirrorP");
            var Q65;
            Q65=sQuery(id+"F6.wireOp",VERTEX,"E74.MirrorP");
            var Q66;
            Q66=sQuery(id+"F6.wireOp",VERTEX,"E132.MirrorP");
            var Q67;
            Q67=sQuery(id+"F6.wireOp",VERTEX,"E99.MirrorP");
            var Q68;
            Q68=sQuery(id+"F6.wireOp",VERTEX,"E170.1.0.1");
            var Q69;
            Q69=sQuery(id+"F6.wireOp",VERTEX,"E163.MirrorP");
            var Q70;
            Q70=sQuery(id+"F6.wireOp",VERTEX,"E170.2.0.1");
            var Q71;
            Q71=sQuery(id+"F6.wireOp",VERTEX,"E118.MirrorP");
            var Q72;
            Q72=makeQuery(id+"F1.opExtrude","SWEPT_BODY",BODY,{"disambiguationData":[OSD([sQuery(id+"F0.wireOp",EDGE,"E0.bottom"),sQuery(id+"F0.wireOp",EDGE,"E0.top"),sQuery(id+"F0.wireOp",EDGE,"E0.left"),sQuery(id+"F0.wireOp",EDGE,"E0.right")])]});
            hole(context, id + "F7", {"style" : HoleStyle.SIMPLE, "endStyle" : HoleEndStyle.THROUGH, "holeDiameter" : 4 * mm, "locations" : qUnion([Q0, Q1, Q2, Q3, Q4, Q5, Q6, Q7, Q8, Q9, Q10, Q11, Q12, Q13, Q14, Q15, Q16, Q17, Q18, Q19, Q20, Q21, Q22, Q23, Q24, Q25, Q26, Q27, Q28, Q29, Q30, Q31, Q32, Q33, Q34, Q35, Q36, Q37, Q38, Q39, Q40, Q41, Q42, Q43, Q44, Q45, Q46, Q47, Q48, Q49, Q50, Q51, Q52, Q53, Q54, Q55, Q56, Q57, Q58, Q59, Q60, Q61, Q62, Q63, Q64, Q65, Q66, Q67, Q68, Q69, Q70, Q71]), "scope" : qUnion([Q72]), "majorDiameter" : 6.35 * mm, "tappedDepth" : 12.7 * mm, "tapClearance" : 3});
        }
        {
            var Q0;
            Q0=sQuery(id+"F6.wireOp",VERTEX,"E10.1.0.2");
            var Q1;
            Q1=sQuery(id+"F6.wireOp",VERTEX,"E17");
            var Q2;
            Q2=sQuery(id+"F6.wireOp",VERTEX,"E10.2.0.8");
            var Q3;
            Q3=sQuery(id+"F6.wireOp",VERTEX,"E10.3.0.7");
            var Q4;
            Q4=sQuery(id+"F6.wireOp",VERTEX,"E190.MirrorP");
            var Q5;
            Q5=sQuery(id+"F6.wireOp",VERTEX,"E10.1.0.8");
            var Q6;
            Q6=sQuery(id+"F6.wireOp",VERTEX,"E10.3.0.6");
            var Q7;
            Q7=sQuery(id+"F6.wireOp",VERTEX,"E210.MirrorP");
            var Q8;
            Q8=sQuery(id+"F6.wireOp",VERTEX,"E195.MirrorP");
            var Q9;
            Q9=sQuery(id+"F6.wireOp",VERTEX,"E222.MirrorP");
            var Q10;
            Q10=sQuery(id+"F6.wireOp",VERTEX,"E219.MirrorP");
            var Q11;
            Q11=sQuery(id+"F6.wireOp",VERTEX,"E207.MirrorP");
            var Q12;
            Q12=sQuery(id+"F6.wireOp",VERTEX,"E9.5.0");
            var Q13;
            Q13=sQuery(id+"F6.wireOp",VERTEX,"E10.2.0.3");
            var Q14;
            Q14=sQuery(id+"F6.wireOp",VERTEX,"E194.MirrorP");
            var Q15;
            Q15=sQuery(id+"F6.wireOp",VERTEX,"E10.1.0.5");
            var Q16;
            Q16=sQuery(id+"F6.wireOp",VERTEX,"E203.MirrorP");
            var Q17;
            Q17=sQuery(id+"F6.wireOp",VERTEX,"E10.2.0.1");
            var Q18;
            Q18=sQuery(id+"F6.wireOp",VERTEX,"E9.1.0");
            var Q19;
            Q19=sQuery(id+"F6.wireOp",VERTEX,"E9.7.0");
            var Q20;
            Q20=sQuery(id+"F6.wireOp",VERTEX,"E213.MirrorP");
            var Q21;
            Q21=sQuery(id+"F6.wireOp",VERTEX,"E10.2.0.4");
            var Q22;
            Q22=sQuery(id+"F6.wireOp",VERTEX,"E197.MirrorP");
            var Q23;
            Q23=sQuery(id+"F6.wireOp",VERTEX,"E9.4.0");
            var Q24;
            Q24=sQuery(id+"F6.wireOp",VERTEX,"E191.MirrorP");
            var Q25;
            Q25=sQuery(id+"F6.wireOp",VERTEX,"E209.MirrorP");
            var Q26;
            Q26=sQuery(id+"F6.wireOp",VERTEX,"E9.3.0");
            var Q27;
            Q27=sQuery(id+"F6.wireOp",VERTEX,"E19");
            var Q28;
            Q28=sQuery(id+"F6.wireOp",VERTEX,"E215.MirrorP");
            var Q29;
            Q29=sQuery(id+"F6.wireOp",VERTEX,"E205.MirrorP");
            var Q30;
            Q30=sQuery(id+"F6.wireOp",VERTEX,"E15");
            var Q31;
            Q31=sQuery(id+"F6.wireOp",VERTEX,"E221.MirrorP");
            var Q32;
            Q32=sQuery(id+"F6.wireOp",VERTEX,"E10.3.0.2");
            var Q33;
            Q33=sQuery(id+"F6.wireOp",VERTEX,"E10.1.0.4");
            var Q34;
            Q34=sQuery(id+"F6.wireOp",VERTEX,"E20");
            var Q35;
            Q35=sQuery(id+"F6.wireOp",VERTEX,"E10.3.0.5");
            var Q36;
            Q36=sQuery(id+"F6.wireOp",VERTEX,"E21");
            var Q37;
            Q37=sQuery(id+"F6.wireOp",VERTEX,"E10.3.0.8");
            var Q38;
            Q38=sQuery(id+"F6.wireOp",VERTEX,"E10.2.0.5");
            var Q39;
            Q39=sQuery(id+"F6.wireOp",VERTEX,"E8");
            var Q40;
            Q40=sQuery(id+"F6.wireOp",VERTEX,"E9.6.0");
            var Q41;
            Q41=sQuery(id+"F6.wireOp",VERTEX,"E204.MirrorP");
            var Q42;
            Q42=sQuery(id+"F6.wireOp",VERTEX,"E18");
            var Q43;
            Q43=sQuery(id+"F6.wireOp",VERTEX,"E188.MirrorP");
            var Q44;
            Q44=sQuery(id+"F6.wireOp",VERTEX,"E200.MirrorP");
            var Q45;
            Q45=sQuery(id+"F6.wireOp",VERTEX,"E10.2.0.2");
            var Q46;
            Q46=sQuery(id+"F6.wireOp",VERTEX,"E217.MirrorP");
            var Q47;
            Q47=sQuery(id+"F6.wireOp",VERTEX,"E10.2.0.6");
            var Q48;
            Q48=sQuery(id+"F6.wireOp",VERTEX,"E10.3.0.4");
            var Q49;
            Q49=sQuery(id+"F6.wireOp",VERTEX,"E10.1.0.6");
            var Q50;
            Q50=sQuery(id+"F6.wireOp",VERTEX,"E22");
            var Q51;
            Q51=sQuery(id+"F6.wireOp",VERTEX,"E187.MirrorP");
            var Q52;
            Q52=sQuery(id+"F6.wireOp",VERTEX,"E218.MirrorP");
            var Q53;
            Q53=sQuery(id+"F6.wireOp",VERTEX,"E10.1.0.3");
            var Q54;
            Q54=sQuery(id+"F6.wireOp",VERTEX,"E184.MirrorP");
            var Q55;
            Q55=sQuery(id+"F6.wireOp",VERTEX,"E16");
            var Q56;
            Q56=sQuery(id+"F6.wireOp",VERTEX,"E10.2.0.7");
            var Q57;
            Q57=sQuery(id+"F6.wireOp",VERTEX,"E10.3.0.3");
            var Q58;
            Q58=sQuery(id+"F6.wireOp",VERTEX,"E208.MirrorP");
            var Q59;
            Q59=sQuery(id+"F6.wireOp",VERTEX,"E198.MirrorP");
            var Q60;
            Q60=sQuery(id+"F6.wireOp",VERTEX,"E211.MirrorP");
            var Q61;
            Q61=sQuery(id+"F6.wireOp",VERTEX,"E223.MirrorP");
            var Q62;
            Q62=sQuery(id+"F6.wireOp",VERTEX,"E10.1.0.1");
            var Q63;
            Q63=sQuery(id+"F6.wireOp",VERTEX,"E189.MirrorP");
            var Q64;
            Q64=sQuery(id+"F6.wireOp",VERTEX,"E186.MirrorP");
            var Q65;
            Q65=sQuery(id+"F6.wireOp",VERTEX,"E202.MirrorP");
            var Q66;
            Q66=sQuery(id+"F6.wireOp",VERTEX,"E192.MirrorP");
            var Q67;
            Q67=sQuery(id+"F6.wireOp",VERTEX,"E10.3.0.1");
            var Q68;
            Q68=sQuery(id+"F6.wireOp",VERTEX,"E10.1.0.7");
            var Q69;
            Q69=sQuery(id+"F6.wireOp",VERTEX,"E212.MirrorP");
            var Q70;
            Q70=sQuery(id+"F6.wireOp",VERTEX,"E9.2.0");
            var Q71;
            Q71=sQuery(id+"F6.wireOp",VERTEX,"E185.MirrorP");
            var Q72;
            Q72=makeQuery(id+"F1.opExtrude","SWEPT_BODY",BODY,{"disambiguationData":[OSD([sQuery(id+"F0.wireOp",EDGE,"E0.bottom"),sQuery(id+"F0.wireOp",EDGE,"E0.top"),sQuery(id+"F0.wireOp",EDGE,"E0.left"),sQuery(id+"F0.wireOp",EDGE,"E0.right")])]});
            hole(context, id + "F8", {"style" : HoleStyle.SIMPLE, "endStyle" : HoleEndStyle.THROUGH, "holeDiameter" : 4 * mm, "locations" : qUnion([Q0, Q1, Q2, Q3, Q4, Q5, Q6, Q7, Q8, Q9, Q10, Q11, Q12, Q13, Q14, Q15, Q16, Q17, Q18, Q19, Q20, Q21, Q22, Q23, Q24, Q25, Q26, Q27, Q28, Q29, Q30, Q31, Q32, Q33, Q34, Q35, Q36, Q37, Q38, Q39, Q40, Q41, Q42, Q43, Q44, Q45, Q46, Q47, Q48, Q49, Q50, Q51, Q52, Q53, Q54, Q55, Q56, Q57, Q58, Q59, Q60, Q61, Q62, Q63, Q64, Q65, Q66, Q67, Q68, Q69, Q70, Q71]), "scope" : qUnion([Q72]), "majorDiameter" : 6.35 * mm, "tappedDepth" : 12.7 * mm, "tapClearance" : 3});
        }
        {
            var Q0;
            Q0=sQuery(id+"F6.wireOp",VERTEX,"E294.MirrorP");
            var Q1;
            Q1=sQuery(id+"F6.wireOp",VERTEX,"E50.MirrorP");
            var Q2;
            Q2=sQuery(id+"F6.wireOp",VERTEX,"E269.MirrorP");
            var Q3;
            Q3=sQuery(id+"F6.wireOp",VERTEX,"E58.MirrorP");
            var Q4;
            Q4=sQuery(id+"F6.wireOp",VERTEX,"E41.MirrorP");
            var Q5;
            Q5=sQuery(id+"F6.wireOp",VERTEX,"E240.MirrorP");
            var Q6;
            Q6=sQuery(id+"F6.wireOp",VERTEX,"E46.MirrorP");
            var Q7;
            Q7=sQuery(id+"F6.wireOp",VERTEX,"E62.MirrorP");
            var Q8;
            Q8=sQuery(id+"F6.wireOp",VERTEX,"E65.MirrorP");
            var Q9;
            Q9=sQuery(id+"F6.wireOp",VERTEX,"E71.MirrorP");
            var Q10;
            Q10=sQuery(id+"F6.wireOp",VERTEX,"E272.MirrorP");
            var Q11;
            Q11=sQuery(id+"F6.wireOp",VERTEX,"E29.MirrorP");
            var Q12;
            Q12=sQuery(id+"F6.wireOp",VERTEX,"E54.MirrorP");
            var Q13;
            Q13=sQuery(id+"F6.wireOp",VERTEX,"E69.MirrorP");
            var Q14;
            Q14=sQuery(id+"F6.wireOp",VERTEX,"E38.MirrorP");
            var Q15;
            Q15=sQuery(id+"F6.wireOp",VERTEX,"E274.MirrorP");
            var Q16;
            Q16=sQuery(id+"F6.wireOp",VERTEX,"E245.MirrorP");
            var Q17;
            Q17=sQuery(id+"F6.wireOp",VERTEX,"E282.MirrorP");
            var Q18;
            Q18=sQuery(id+"F6.wireOp",VERTEX,"E226.MirrorP");
            var Q19;
            Q19=sQuery(id+"F6.wireOp",VERTEX,"E35.MirrorP");
            var Q20;
            Q20=sQuery(id+"F6.wireOp",VERTEX,"E40.MirrorP");
            var Q21;
            Q21=sQuery(id+"F6.wireOp",VERTEX,"E48.MirrorP");
            var Q22;
            Q22=sQuery(id+"F6.wireOp",VERTEX,"E285.MirrorP");
            var Q23;
            Q23=sQuery(id+"F6.wireOp",VERTEX,"E32.MirrorP");
            var Q24;
            Q24=sQuery(id+"F6.wireOp",VERTEX,"E231.MirrorP");
            var Q25;
            Q25=sQuery(id+"F6.wireOp",VERTEX,"E52.MirrorP");
            var Q26;
            Q26=sQuery(id+"F6.wireOp",VERTEX,"E59.MirrorP");
            var Q27;
            Q27=sQuery(id+"F6.wireOp",VERTEX,"E37.MirrorP");
            var Q28;
            Q28=sQuery(id+"F6.wireOp",VERTEX,"E53.MirrorP");
            var Q29;
            Q29=sQuery(id+"F6.wireOp",VERTEX,"E47.MirrorP");
            var Q30;
            Q30=sQuery(id+"F6.wireOp",VERTEX,"E242.MirrorP");
            var Q31;
            Q31=sQuery(id+"F6.wireOp",VERTEX,"E61.MirrorP");
            var Q32;
            Q32=sQuery(id+"F6.wireOp",VERTEX,"E45.MirrorP");
            var Q33;
            Q33=sQuery(id+"F6.wireOp",VERTEX,"E289.MirrorP");
            var Q34;
            Q34=sQuery(id+"F6.wireOp",VERTEX,"E293.MirrorP");
            var Q35;
            Q35=sQuery(id+"F6.wireOp",VERTEX,"E265.MirrorP");
            var Q36;
            Q36=sQuery(id+"F6.wireOp",VERTEX,"E290.MirrorP");
            var Q37;
            Q37=sQuery(id+"F6.wireOp",VERTEX,"E44.MirrorP");
            var Q38;
            Q38=sQuery(id+"F6.wireOp",VERTEX,"E36.MirrorP");
            var Q39;
            Q39=sQuery(id+"F6.wireOp",VERTEX,"E254.MirrorP");
            var Q40;
            Q40=sQuery(id+"F6.wireOp",VERTEX,"E70.MirrorP");
            var Q41;
            Q41=sQuery(id+"F6.wireOp",VERTEX,"E55.MirrorP");
            var Q42;
            Q42=sQuery(id+"F6.wireOp",VERTEX,"E39.MirrorP");
            var Q43;
            Q43=sQuery(id+"F6.wireOp",VERTEX,"E256.MirrorP");
            var Q44;
            Q44=sQuery(id+"F6.wireOp",VERTEX,"E227.MirrorP");
            var Q45;
            Q45=sQuery(id+"F6.wireOp",VERTEX,"E63.MirrorP");
            var Q46;
            Q46=sQuery(id+"F6.wireOp",VERTEX,"E224.MirrorP");
            var Q47;
            Q47=sQuery(id+"F6.wireOp",VERTEX,"E300.MirrorP");
            var Q48;
            Q48=sQuery(id+"F6.wireOp",VERTEX,"E33.MirrorP");
            var Q49;
            Q49=sQuery(id+"F6.wireOp",VERTEX,"E230.MirrorP");
            var Q50;
            Q50=sQuery(id+"F6.wireOp",VERTEX,"E301.MirrorP");
            var Q51;
            Q51=sQuery(id+"F6.wireOp",VERTEX,"E288.MirrorP");
            var Q52;
            Q52=sQuery(id+"F6.wireOp",VERTEX,"E273.MirrorP");
            var Q53;
            Q53=sQuery(id+"F6.wireOp",VERTEX,"E259.MirrorP");
            var Q54;
            Q54=sQuery(id+"F6.wireOp",VERTEX,"E51.MirrorP");
            var Q55;
            Q55=sQuery(id+"F6.wireOp",VERTEX,"E66.MirrorP");
            var Q56;
            Q56=sQuery(id+"F6.wireOp",VERTEX,"E292.MirrorP");
            var Q57;
            Q57=sQuery(id+"F6.wireOp",VERTEX,"E232.MirrorP");
            var Q58;
            Q58=sQuery(id+"F6.wireOp",VERTEX,"E262.MirrorP");
            var Q59;
            Q59=sQuery(id+"F6.wireOp",VERTEX,"E34.MirrorP");
            var Q60;
            Q60=sQuery(id+"F6.wireOp",VERTEX,"E26.MirrorP");
            var Q61;
            Q61=sQuery(id+"F6.wireOp",VERTEX,"E57.MirrorP");
            var Q62;
            Q62=sQuery(id+"F6.wireOp",VERTEX,"E25.MirrorP");
            var Q63;
            Q63=sQuery(id+"F6.wireOp",VERTEX,"E258.MirrorP");
            var Q64;
            Q64=sQuery(id+"F6.wireOp",VERTEX,"E238.MirrorP");
            var Q65;
            Q65=sQuery(id+"F6.wireOp",VERTEX,"E235.MirrorP");
            var Q66;
            Q66=sQuery(id+"F6.wireOp",VERTEX,"E43.MirrorP");
            var Q67;
            Q67=sQuery(id+"F6.wireOp",VERTEX,"E68.MirrorP");
            var Q68;
            Q68=sQuery(id+"F6.wireOp",VERTEX,"E268.MirrorP");
            var Q69;
            Q69=sQuery(id+"F6.wireOp",VERTEX,"E67.MirrorP");
            var Q70;
            Q70=sQuery(id+"F6.wireOp",VERTEX,"E56.MirrorP");
            var Q71;
            Q71=sQuery(id+"F6.wireOp",VERTEX,"E23.MirrorP");
            var Q72;
            Q72=makeQuery(id+"F1.opExtrude","SWEPT_BODY",BODY,{"disambiguationData":[OSD([sQuery(id+"F0.wireOp",EDGE,"E0.bottom"),sQuery(id+"F0.wireOp",EDGE,"E0.top"),sQuery(id+"F0.wireOp",EDGE,"E0.left"),sQuery(id+"F0.wireOp",EDGE,"E0.right")])]});
            hole(context, id + "F9", {"style" : HoleStyle.SIMPLE, "endStyle" : HoleEndStyle.THROUGH, "holeDiameter" : 4 * mm, "locations" : qUnion([Q0, Q1, Q2, Q3, Q4, Q5, Q6, Q7, Q8, Q9, Q10, Q11, Q12, Q13, Q14, Q15, Q16, Q17, Q18, Q19, Q20, Q21, Q22, Q23, Q24, Q25, Q26, Q27, Q28, Q29, Q30, Q31, Q32, Q33, Q34, Q35, Q36, Q37, Q38, Q39, Q40, Q41, Q42, Q43, Q44, Q45, Q46, Q47, Q48, Q49, Q50, Q51, Q52, Q53, Q54, Q55, Q56, Q57, Q58, Q59, Q60, Q61, Q62, Q63, Q64, Q65, Q66, Q67, Q68, Q69, Q70, Q71]), "scope" : qUnion([Q72]), "majorDiameter" : 6.35 * mm, "tappedDepth" : 12.7 * mm, "tapClearance" : 3});
        }
        {
            var Q0;
            Q0=sQuery(id+"F6.wireOp",VERTEX,"E284.MirrorP");
            var Q1;
            Q1=sQuery(id+"F6.wireOp",VERTEX,"E297.MirrorP");
            var Q2;
            Q2=sQuery(id+"F6.wireOp",VERTEX,"E237.MirrorP");
            var Q3;
            Q3=sQuery(id+"F6.wireOp",VERTEX,"E252.MirrorP");
            var Q4;
            Q4=sQuery(id+"F6.wireOp",VERTEX,"E281.MirrorP");
            var Q5;
            Q5=sQuery(id+"F6.wireOp",VERTEX,"E168.MirrorP");
            var Q6;
            Q6=sQuery(id+"F6.wireOp",VERTEX,"E255.MirrorP");
            var Q7;
            Q7=sQuery(id+"F6.wireOp",VERTEX,"E136.MirrorP");
            var Q8;
            Q8=sQuery(id+"F6.wireOp",VERTEX,"E72.MirrorP");
            var Q9;
            Q9=sQuery(id+"F6.wireOp",VERTEX,"E137.MirrorP");
            var Q10;
            Q10=sQuery(id+"F6.wireOp",VERTEX,"E121.MirrorP");
            var Q11;
            Q11=sQuery(id+"F6.wireOp",VERTEX,"E169.MirrorP");
            var Q12;
            Q12=sQuery(id+"F6.wireOp",VERTEX,"E287.MirrorP");
            var Q13;
            Q13=sQuery(id+"F6.wireOp",VERTEX,"E141.MirrorP");
            var Q14;
            Q14=sQuery(id+"F6.wireOp",VERTEX,"E109.MirrorP");
            var Q15;
            Q15=sQuery(id+"F6.wireOp",VERTEX,"E94.MirrorP");
            var Q16;
            Q16=sQuery(id+"F6.wireOp",VERTEX,"E114.MirrorP");
            var Q17;
            Q17=sQuery(id+"F6.wireOp",VERTEX,"E160.MirrorP");
            var Q18;
            Q18=sQuery(id+"F6.wireOp",VERTEX,"E128.MirrorP");
            var Q19;
            Q19=sQuery(id+"F6.wireOp",VERTEX,"E112.MirrorP");
            var Q20;
            Q20=sQuery(id+"F6.wireOp",VERTEX,"E279.MirrorP");
            var Q21;
            Q21=sQuery(id+"F6.wireOp",VERTEX,"E260.MirrorP");
            var Q22;
            Q22=sQuery(id+"F6.wireOp",VERTEX,"E126.MirrorP");
            var Q23;
            Q23=sQuery(id+"F6.wireOp",VERTEX,"E283.MirrorP");
            var Q24;
            Q24=sQuery(id+"F6.wireOp",VERTEX,"E264.MirrorP");
            var Q25;
            Q25=sQuery(id+"F6.wireOp",VERTEX,"E147.MirrorP");
            var Q26;
            Q26=sQuery(id+"F6.wireOp",VERTEX,"E138.MirrorP");
            var Q27;
            Q27=sQuery(id+"F6.wireOp",VERTEX,"E122.MirrorP");
            var Q28;
            Q28=sQuery(id+"F6.wireOp",VERTEX,"E236.MirrorP");
            var Q29;
            Q29=sQuery(id+"F6.wireOp",VERTEX,"E159.MirrorP");
            var Q30;
            Q30=sQuery(id+"F6.wireOp",VERTEX,"E143.MirrorP");
            var Q31;
            Q31=sQuery(id+"F6.wireOp",VERTEX,"E88.MirrorP");
            var Q32;
            Q32=sQuery(id+"F6.wireOp",VERTEX,"E124.MirrorP");
            var Q33;
            Q33=sQuery(id+"F6.wireOp",VERTEX,"E157.MirrorP");
            var Q34;
            Q34=sQuery(id+"F6.wireOp",VERTEX,"E291.MirrorP");
            var Q35;
            Q35=sQuery(id+"F6.wireOp",VERTEX,"E166.MirrorP");
            var Q36;
            Q36=sQuery(id+"F6.wireOp",VERTEX,"E225.MirrorP");
            var Q37;
            Q37=sQuery(id+"F6.wireOp",VERTEX,"E295.MirrorP");
            var Q38;
            Q38=sQuery(id+"F6.wireOp",VERTEX,"E298.MirrorP");
            var Q39;
            Q39=sQuery(id+"F6.wireOp",VERTEX,"E270.MirrorP");
            var Q40;
            Q40=sQuery(id+"F6.wireOp",VERTEX,"E296.MirrorP");
            var Q41;
            Q41=sQuery(id+"F6.wireOp",VERTEX,"E134.MirrorP");
            var Q42;
            Q42=sQuery(id+"F6.wireOp",VERTEX,"E280.MirrorP");
            var Q43;
            Q43=sQuery(id+"F6.wireOp",VERTEX,"E266.MirrorP");
            var Q44;
            Q44=sQuery(id+"F6.wireOp",VERTEX,"E100.MirrorP");
            var Q45;
            Q45=sQuery(id+"F6.wireOp",VERTEX,"E164.MirrorP");
            var Q46;
            Q46=sQuery(id+"F6.wireOp",VERTEX,"E148.MirrorP");
            var Q47;
            Q47=sQuery(id+"F6.wireOp",VERTEX,"E158.MirrorP");
            var Q48;
            Q48=sQuery(id+"F6.wireOp",VERTEX,"E135.MirrorP");
            var Q49;
            Q49=sQuery(id+"F6.wireOp",VERTEX,"E107.MirrorP");
            var Q50;
            Q50=sQuery(id+"F6.wireOp",VERTEX,"E286.MirrorP");
            var Q51;
            Q51=sQuery(id+"F6.wireOp",VERTEX,"E263.MirrorP");
            var Q52;
            Q52=sQuery(id+"F6.wireOp",VERTEX,"E271.MirrorP");
            var Q53;
            Q53=sQuery(id+"F6.wireOp",VERTEX,"E101.MirrorP");
            var Q54;
            Q54=sQuery(id+"F6.wireOp",VERTEX,"E150.MirrorP");
            var Q55;
            Q55=sQuery(id+"F6.wireOp",VERTEX,"E229.MirrorP");
            var Q56;
            Q56=sQuery(id+"F6.wireOp",VERTEX,"E276.MirrorP");
            var Q57;
            Q57=sQuery(id+"F6.wireOp",VERTEX,"E129.MirrorP");
            var Q58;
            Q58=sQuery(id+"F6.wireOp",VERTEX,"E104.MirrorP");
            var Q59;
            Q59=sQuery(id+"F6.wireOp",VERTEX,"E278.MirrorP");
            var Q60;
            Q60=sQuery(id+"F6.wireOp",VERTEX,"E233.MirrorP");
            var Q61;
            Q61=sQuery(id+"F6.wireOp",VERTEX,"E248.MirrorP");
            var Q62;
            Q62=sQuery(id+"F6.wireOp",VERTEX,"E84.MirrorP");
            var Q63;
            Q63=sQuery(id+"F6.wireOp",VERTEX,"E98.MirrorP");
            var Q64;
            Q64=sQuery(id+"F6.wireOp",VERTEX,"E250.MirrorP");
            var Q65;
            Q65=sQuery(id+"F6.wireOp",VERTEX,"E249.MirrorP");
            var Q66;
            Q66=sQuery(id+"F6.wireOp",VERTEX,"E115.MirrorP");
            var Q67;
            Q67=sQuery(id+"F6.wireOp",VERTEX,"E239.MirrorP");
            var Q68;
            Q68=sQuery(id+"F6.wireOp",VERTEX,"E119.MirrorP");
            var Q69;
            Q69=sQuery(id+"F6.wireOp",VERTEX,"E277.MirrorP");
            var Q70;
            Q70=sQuery(id+"F6.wireOp",VERTEX,"E102.MirrorP");
            var Q71;
            Q71=sQuery(id+"F6.wireOp",VERTEX,"E162.MirrorP");
            var Q72;
            Q72=makeQuery(id+"F1.opExtrude","SWEPT_BODY",BODY,{"disambiguationData":[OSD([sQuery(id+"F0.wireOp",EDGE,"E0.bottom"),sQuery(id+"F0.wireOp",EDGE,"E0.top"),sQuery(id+"F0.wireOp",EDGE,"E0.left"),sQuery(id+"F0.wireOp",EDGE,"E0.right")])]});
            hole(context, id + "F10", {"style" : HoleStyle.SIMPLE, "endStyle" : HoleEndStyle.THROUGH, "holeDiameter" : 4 * mm, "locations" : qUnion([Q0, Q1, Q2, Q3, Q4, Q5, Q6, Q7, Q8, Q9, Q10, Q11, Q12, Q13, Q14, Q15, Q16, Q17, Q18, Q19, Q20, Q21, Q22, Q23, Q24, Q25, Q26, Q27, Q28, Q29, Q30, Q31, Q32, Q33, Q34, Q35, Q36, Q37, Q38, Q39, Q40, Q41, Q42, Q43, Q44, Q45, Q46, Q47, Q48, Q49, Q50, Q51, Q52, Q53, Q54, Q55, Q56, Q57, Q58, Q59, Q60, Q61, Q62, Q63, Q64, Q65, Q66, Q67, Q68, Q69, Q70, Q71]), "scope" : qUnion([Q72]), "majorDiameter" : 6.35 * mm, "tappedDepth" : 12.7 * mm, "tapClearance" : 3});
        }
        {
            var Q0;
            Q0=sQuery(id+"F6.wireOp",VERTEX,"E80.MirrorP");
            var Q1;
            Q1=sQuery(id+"F6.wireOp",VERTEX,"E175");
            var Q2;
            Q2=sQuery(id+"F6.wireOp",VERTEX,"E170.1.0.0");
            var Q3;
            Q3=sQuery(id+"F6.wireOp",VERTEX,"E172");
            var Q4;
            Q4=sQuery(id+"F6.wireOp",VERTEX,"E170.2.0.0");
            var Q5;
            Q5=sQuery(id+"F6.wireOp",VERTEX,"E176");
            var Q6;
            Q6=sQuery(id+"F6.wireOp",VERTEX,"E171.0.3.0");
            var Q7;
            Q7=sQuery(id+"F6.wireOp",VERTEX,"E177");
            var Q8;
            Q8=sQuery(id+"F6.wireOp",VERTEX,"E199.MirrorP");
            var Q9;
            Q9=sQuery(id+"F6.wireOp",VERTEX,"E220.MirrorP");
            var Q10;
            Q10=sQuery(id+"F6.wireOp",VERTEX,"E216.MirrorP");
            var Q11;
            Q11=sQuery(id+"F6.wireOp",VERTEX,"E206.MirrorP");
            var Q12;
            Q12=sQuery(id+"F6.wireOp",VERTEX,"E193.MirrorP");
            var Q13;
            Q13=sQuery(id+"F6.wireOp",VERTEX,"E196.MirrorP");
            var Q14;
            Q14=sQuery(id+"F6.wireOp",VERTEX,"E214.MirrorP");
            var Q15;
            Q15=sQuery(id+"F6.wireOp",VERTEX,"E7");
            var Q16;
            Q16=sQuery(id+"F6.wireOp",VERTEX,"E11");
            var Q17;
            Q17=sQuery(id+"F6.wireOp",VERTEX,"E10.1.0.0");
            var Q18;
            Q18=sQuery(id+"F6.wireOp",VERTEX,"E12");
            var Q19;
            Q19=sQuery(id+"F6.wireOp",VERTEX,"E10.2.0.0");
            var Q20;
            Q20=sQuery(id+"F6.wireOp",VERTEX,"E14");
            var Q21;
            Q21=sQuery(id+"F6.wireOp",VERTEX,"E10.3.0.0");
            var Q22;
            Q22=sQuery(id+"F6.wireOp",VERTEX,"E13");
            var Q23;
            Q23=sQuery(id+"F6.wireOp",VERTEX,"E60.MirrorP");
            var Q24;
            Q24=sQuery(id+"F6.wireOp",VERTEX,"E28.MirrorP");
            var Q25;
            Q25=sQuery(id+"F6.wireOp",VERTEX,"E49.MirrorP");
            var Q26;
            Q26=sQuery(id+"F6.wireOp",VERTEX,"E42.MirrorP");
            var Q27;
            Q27=sQuery(id+"F6.wireOp",VERTEX,"E27.MirrorP");
            var Q28;
            Q28=sQuery(id+"F6.wireOp",VERTEX,"E64.MirrorP");
            var Q29;
            Q29=sQuery(id+"F6.wireOp",VERTEX,"E31.MirrorP");
            var Q30;
            Q30=sQuery(id+"F6.wireOp",VERTEX,"E30.MirrorP");
            var Q31;
            Q31=sQuery(id+"F6.wireOp",VERTEX,"E257.MirrorP");
            var Q32;
            Q32=sQuery(id+"F6.wireOp",VERTEX,"E253.MirrorP");
            var Q33;
            Q33=sQuery(id+"F6.wireOp",VERTEX,"E243.MirrorP");
            var Q34;
            Q34=sQuery(id+"F6.wireOp",VERTEX,"E241.MirrorP");
            var Q35;
            Q35=sQuery(id+"F6.wireOp",VERTEX,"E299.MirrorP");
            var Q36;
            Q36=sQuery(id+"F6.wireOp",VERTEX,"E228.MirrorP");
            var Q37;
            Q37=sQuery(id+"F6.wireOp",VERTEX,"E261.MirrorP");
            var Q38;
            Q38=sQuery(id+"F6.wireOp",VERTEX,"E234.MirrorP");
            var Q39;
            Q39=sQuery(id+"F6.wireOp",VERTEX,"E244.MirrorP");
            var Q40;
            Q40=sQuery(id+"F6.wireOp",VERTEX,"E267.MirrorP");
            var Q41;
            Q41=sQuery(id+"F6.wireOp",VERTEX,"E246.MirrorP");
            var Q42;
            Q42=sQuery(id+"F6.wireOp",VERTEX,"E275.MirrorP");
            var Q43;
            Q43=sQuery(id+"F6.wireOp",VERTEX,"E247.MirrorP");
            var Q44;
            Q44=sQuery(id+"F6.wireOp",VERTEX,"E251.MirrorP");
            var Q45;
            Q45=sQuery(id+"F6.wireOp",VERTEX,"E77.MirrorP");
            var Q46;
            Q46=sQuery(id+"F6.wireOp",VERTEX,"E87.MirrorP");
            var Q47;
            Q47=sQuery(id+"F6.wireOp",VERTEX,"E81.MirrorP");
            var Q48;
            Q48=sQuery(id+"F6.wireOp",VERTEX,"E127.MirrorP");
            var Q49;
            Q49=sQuery(id+"F6.wireOp",VERTEX,"E92.MirrorP");
            var Q50;
            Q50=sQuery(id+"F6.wireOp",VERTEX,"E93.MirrorP");
            var Q51;
            Q51=sQuery(id+"F6.wireOp",VERTEX,"E123.MirrorP");
            var Q52;
            Q52=sQuery(id+"F6.wireOp",VERTEX,"E125.MirrorP");
            var Q53;
            Q53=sQuery(id+"F6.wireOp",VERTEX,"E90.MirrorP");
            var Q54;
            Q54=sQuery(id+"F6.wireOp",VERTEX,"E76.MirrorP");
            var Q55;
            Q55=sQuery(id+"F6.wireOp",VERTEX,"E96.MirrorP");
            var Q56;
            Q56=sQuery(id+"F6.wireOp",VERTEX,"E113.MirrorP");
            var Q57;
            Q57=sQuery(id+"F6.wireOp",VERTEX,"E73.MirrorP");
            var Q58;
            Q58=sQuery(id+"F6.wireOp",VERTEX,"E86.MirrorP");
            var Q59;
            Q59=sQuery(id+"F6.wireOp",VERTEX,"E149.MirrorP");
            var Q60;
            Q60=makeQuery(id+"F1.opExtrude","SWEPT_BODY",BODY,{"disambiguationData":[OSD([sQuery(id+"F0.wireOp",EDGE,"E0.bottom"),sQuery(id+"F0.wireOp",EDGE,"E0.top"),sQuery(id+"F0.wireOp",EDGE,"E0.left"),sQuery(id+"F0.wireOp",EDGE,"E0.right")])]});
            hole(context, id + "F11", {"style" : HoleStyle.SIMPLE, "endStyle" : HoleEndStyle.THROUGH, "holeDiameter" : 8 * mm, "locations" : qUnion([Q0, Q1, Q2, Q3, Q4, Q5, Q6, Q7, Q8, Q9, Q10, Q11, Q12, Q13, Q14, Q15, Q16, Q17, Q18, Q19, Q20, Q21, Q22, Q23, Q24, Q25, Q26, Q27, Q28, Q29, Q30, Q31, Q32, Q33, Q34, Q35, Q36, Q37, Q38, Q39, Q40, Q41, Q42, Q43, Q44, Q45, Q46, Q47, Q48, Q49, Q50, Q51, Q52, Q53, Q54, Q55, Q56, Q57, Q58, Q59]), "scope" : qUnion([Q60]), "majorDiameter" : 6.35 * mm, "tappedDepth" : 12.7 * mm, "tapClearance" : 3});
        }
    });
